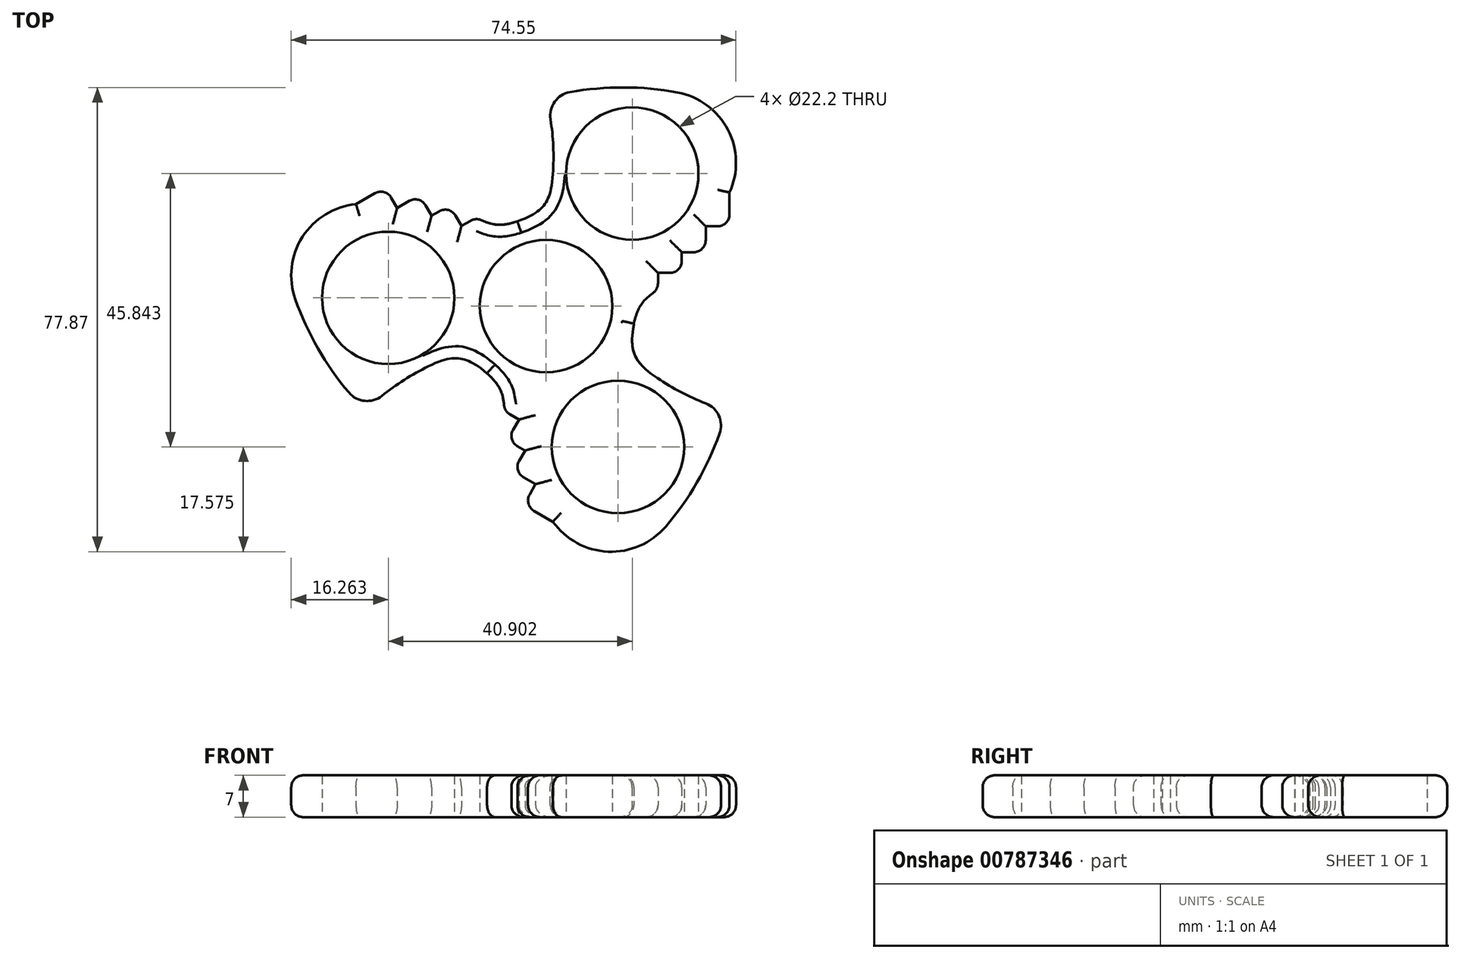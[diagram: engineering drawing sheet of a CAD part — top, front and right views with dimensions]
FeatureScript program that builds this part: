
annotation { "Feature Type Name" : "Feature", "Feature Type Description" : "" }
export const myFeature = defineFeature(function(context is Context, id is Id, definition is map)
    precondition{}
    {
        {
            var Q0;
            Q0=qCreatedBy(makeId("Top.planeOp"),FACE);
            var sketch = newSketch(context, id + "F0", { "sketchPlane" : qUnion([Q0])});
            skCircle(sketch, "E0", {"center": v(0, 0) * mm, "radius": 15 * mm});
            skArc(sketch, "E1", {"start": v(0, 15) * mm, "mid": v(1.23, 25) * mm, "end": v(0, 35) * mm});
            skPoint(sketch, "E2", {"position": v(0, 15) * mm});
            skPoint(sketch, "E3", {"position": v(0, 35) * mm});
            skPoint(sketch, "E4", {"position": v(36, 31) * mm});
            skArc(sketch, "E5.trimOffspring", {"start": v(36, 31) * mm, "mid": v(18.37, 36.37) * mm, "end": v(0, 35) * mm});
            skArc(sketch, "E6.trimOffspring", {"start": v(14.74, 2.75) * mm, "mid": v(27.95, 14.94) * mm, "end": v(36, 31) * mm});
            skCircle(sketch, "E7", {"center": v(0, 0) * mm, "radius": 11.1 * mm});
            skLineSegment(sketch, "E8", {"start": v(0, 15) * mm, "end": v(14.74, 2.75) * mm, "construction": true});
            skLineSegment(sketch, "E9", {"start": v(36, 31) * mm, "end": v(0, 35) * mm, "construction": true});
            skLineSegment(sketch, "E10", {"start": v(14.74, 2.75) * mm, "end": v(18.74, 2.75) * mm});
            skLineSegment(sketch, "E11", {"start": v(18.74, 2.75) * mm, "end": v(18.74, 5.57) * mm});
            skLineSegment(sketch, "E12", {"start": v(18.74, 5.57) * mm, "end": v(22.74, 5.57) * mm});
            skLineSegment(sketch, "E13", {"start": v(22.74, 5.57) * mm, "end": v(22.74, 9.04) * mm});
            skLineSegment(sketch, "E14", {"start": v(22.74, 9.04) * mm, "end": v(26.74, 9.04) * mm});
            skLineSegment(sketch, "E15", {"start": v(26.74, 9.04) * mm, "end": v(26.74, 13.4) * mm});
            skLineSegment(sketch, "E16", {"start": v(26.74, 13.4) * mm, "end": v(30.74, 13.4) * mm});
            skLineSegment(sketch, "E17", {"start": v(30.74, 13.4) * mm, "end": v(30.74, 19.06) * mm});
            skCircle(sketch, "E18", {"center": v(14.43, 22.23) * mm, "radius": 11.1 * mm});
            skLineSegment(sketch, "E19", {"start": v(0, 0) * mm, "end": v(21.2, 32.64) * mm, "construction": true});
            skPoint(sketch, "E20.1.0", {"position": v(-44.85, 15.68) * mm});
            skLineSegment(sketch, "E20.1.1", {"start": v(-44.85, 15.68) * mm, "end": v(-30.31, -17.5) * mm, "construction": true});
            skArc(sketch, "E20.1.2", {"start": v(-9.76, 11.4) * mm, "mid": v(-26.91, 16.74) * mm, "end": v(-44.85, 15.68) * mm});
            skLineSegment(sketch, "E20.1.3", {"start": v(-9.76, 11.4) * mm, "end": v(-11.76, 14.86) * mm});
            skPoint(sketch, "E20.1.4", {"position": v(-13, -7.5) * mm});
            skArc(sketch, "E20.1.5", {"start": v(-44.85, 15.68) * mm, "mid": v(-40.69, -2.27) * mm, "end": v(-30.31, -17.5) * mm});
            skPoint(sketch, "E20.1.7", {"position": v(-30.31, -17.5) * mm});
            skLineSegment(sketch, "E20.1.8", {"start": v(-13, -7.5) * mm, "end": v(-9.76, 11.4) * mm, "construction": true});
            skLineSegment(sketch, "E20.1.9", {"start": v(-26.97, 19.93) * mm, "end": v(-31.88, 17.1) * mm});
            skCircle(sketch, "E20.1.10", {"center": v(-26.47, 1.39) * mm, "radius": 11.1 * mm});
            skLineSegment(sketch, "E20.1.11", {"start": v(0, 0) * mm, "end": v(-38.87, 2.04) * mm, "construction": true});
            skArc(sketch, "E20.1.12", {"start": v(-13, -7.5) * mm, "mid": v(-22.27, -11.43) * mm, "end": v(-30.31, -17.5) * mm});
            skLineSegment(sketch, "E20.1.14", {"start": v(-19.2, 15.18) * mm, "end": v(-21.2, 18.64) * mm});
            skLineSegment(sketch, "E20.1.15", {"start": v(-14.2, 13.45) * mm, "end": v(-16.2, 16.91) * mm});
            skLineSegment(sketch, "E20.1.16", {"start": v(-16.2, 16.91) * mm, "end": v(-19.2, 15.18) * mm});
            skLineSegment(sketch, "E20.1.17", {"start": v(-11.76, 14.86) * mm, "end": v(-14.2, 13.45) * mm});
            skLineSegment(sketch, "E20.1.19", {"start": v(-24.97, 16.46) * mm, "end": v(-26.97, 19.93) * mm});
            skLineSegment(sketch, "E20.1.20", {"start": v(-21.2, 18.64) * mm, "end": v(-24.97, 16.46) * mm});
            skPoint(sketch, "E20.2.0", {"position": v(8.85, -46.68) * mm});
            skLineSegment(sketch, "E20.2.1", {"start": v(8.85, -46.68) * mm, "end": v(30.31, -17.5) * mm, "construction": true});
            skArc(sketch, "E20.2.2", {"start": v(-4.99, -14.15) * mm, "mid": v(-1.04, -31.68) * mm, "end": v(8.85, -46.68) * mm});
            skLineSegment(sketch, "E20.2.3", {"start": v(-4.99, -14.15) * mm, "end": v(-6.99, -17.61) * mm});
            skPoint(sketch, "E20.2.4", {"position": v(13, -7.5) * mm});
            skArc(sketch, "E20.2.5", {"start": v(8.85, -46.68) * mm, "mid": v(22.31, -34.1) * mm, "end": v(30.31, -17.5) * mm});
            skPoint(sketch, "E20.2.7", {"position": v(30.31, -17.5) * mm});
            skLineSegment(sketch, "E20.2.8", {"start": v(13, -7.5) * mm, "end": v(-4.99, -14.15) * mm, "construction": true});
            skLineSegment(sketch, "E20.2.9", {"start": v(-3.77, -33.32) * mm, "end": v(1.13, -36.16) * mm});
            skCircle(sketch, "E20.2.10", {"center": v(12.03, -23.61) * mm, "radius": 11.1 * mm});
            skLineSegment(sketch, "E20.2.11", {"start": v(0, 0) * mm, "end": v(17.67, -34.68) * mm, "construction": true});
            skArc(sketch, "E20.2.12", {"start": v(13, -7.5) * mm, "mid": v(21.04, -13.57) * mm, "end": v(30.31, -17.5) * mm});
            skLineSegment(sketch, "E20.2.14", {"start": v(-3.54, -24.22) * mm, "end": v(-5.54, -27.68) * mm});
            skLineSegment(sketch, "E20.2.15", {"start": v(-4.55, -19.02) * mm, "end": v(-6.55, -22.48) * mm});
            skLineSegment(sketch, "E20.2.16", {"start": v(-6.55, -22.48) * mm, "end": v(-3.54, -24.22) * mm});
            skLineSegment(sketch, "E20.2.17", {"start": v(-6.99, -17.61) * mm, "end": v(-4.55, -19.02) * mm});
            skLineSegment(sketch, "E20.2.19", {"start": v(-1.77, -29.86) * mm, "end": v(-3.77, -33.32) * mm});
            skLineSegment(sketch, "E20.2.20", {"start": v(-5.54, -27.68) * mm, "end": v(-1.77, -29.86) * mm});
            skSolve(sketch);
        }
        {
            var Q0;
            Q0=qSketchRegion(id+"F0",true);
            extrude(context, id + "F1", {"entities" : qUnion([Q0]), "depth" : 7 * mm, "offsetDistance" : 25 * mm});
        }
        {
            var Q0;
            Q0=makeQuery(id+"F1.opExtrude","SWEPT_EDGE",EDGE,{"disambiguationData":[OSD([sQuery(id+"F0.wireOp",EDGE,"E5.trimOffspring"),sQuery(id+"F0.wireOp",EDGE,"E6.trimOffspring")])]});
            var Q1;
            Q1=makeQuery(id+"F1.opExtrude","SWEPT_EDGE",EDGE,{"disambiguationData":[OSD([sQuery(id+"F0.wireOp",EDGE,"E20.2.2"),sQuery(id+"F0.wireOp",EDGE,"E20.2.5")])]});
            var Q2;
            Q2=makeQuery(id+"F1.opExtrude","SWEPT_EDGE",EDGE,{"disambiguationData":[OSD([sQuery(id+"F0.wireOp",EDGE,"E20.1.2"),sQuery(id+"F0.wireOp",EDGE,"E20.1.5")])]});
            fillet(context, id + "F2", {"entities" : qUnion([Q0, Q1, Q2]), "radius" : 12 * mm, "tangentPropagation" : true, "allowEdgeOverflow" : false});
        }
        {
            var Q0;
            Q0=makeQuery(id+"F1.opExtrude","SWEPT_EDGE",EDGE,{"disambiguationData":[OSD([sQuery(id+"F0.wireOp",EDGE,"E1"),sQuery(id+"F0.wireOp",EDGE,"E5.trimOffspring")])]});
            var Q1;
            Q1=makeQuery(id+"F1.opExtrude","SWEPT_EDGE",EDGE,{"disambiguationData":[OSD([sQuery(id+"F0.wireOp",EDGE,"E20.1.5"),sQuery(id+"F0.wireOp",EDGE,"E20.1.12")])]});
            var Q2;
            Q2=makeQuery(id+"F1.opExtrude","SWEPT_EDGE",EDGE,{"disambiguationData":[OSD([sQuery(id+"F0.wireOp",EDGE,"E20.2.5"),sQuery(id+"F0.wireOp",EDGE,"E20.2.12")])]});
            fillet(context, id + "F3", {"entities" : qUnion([Q0, Q1, Q2]), "radius" : 4 * mm, "tangentPropagation" : true, "allowEdgeOverflow" : false});
        }
        {
            var Q0;
            Q0=makeQuery(id+"F1.opExtrude","SWEPT_EDGE",EDGE,{"disambiguationData":[OSD([sQuery(id+"F0.wireOp",EDGE,"E0"),sQuery(id+"F0.wireOp",EDGE,"544d86c7-8deb-4338-a2d6-1758b23e3787.1.16")])]});
            var Q1;
            Q1=makeQuery(id+"F1.opExtrude","SWEPT_EDGE",EDGE,{"disambiguationData":[OSD([sQuery(id+"F0.wireOp",EDGE,"E0"),sQuery(id+"F0.wireOp",EDGE,"544d86c7-8deb-4338-a2d6-1758b23e3787.2.5")])]});
            var Q2;
            Q2=makeQuery(id+"F1.opExtrude","SWEPT_EDGE",EDGE,{"disambiguationData":[OSD([sQuery(id+"F0.wireOp",EDGE,"E0"),sQuery(id+"F0.wireOp",EDGE,"544d86c7-8deb-4338-a2d6-1758b23e3787.1.5")])]});
            var Q3;
            Q3=makeQuery(id+"F1.opExtrude","SWEPT_EDGE",EDGE,{"disambiguationData":[OSD([sQuery(id+"F0.wireOp",EDGE,"E0"),sQuery(id+"F0.wireOp",EDGE,"E1")])]});
            var Q4;
            Q4=makeQuery(id+"F1.opExtrude","SWEPT_EDGE",EDGE,{"disambiguationData":[OSD([sQuery(id+"F0.wireOp",EDGE,"E0"),sQuery(id+"F0.wireOp",EDGE,"E6.trimOffspring")])]});
            var Q5;
            Q5=makeQuery(id+"F1.opExtrude","SWEPT_EDGE",EDGE,{"disambiguationData":[OSD([sQuery(id+"F0.wireOp",EDGE,"E0"),sQuery(id+"F0.wireOp",EDGE,"544d86c7-8deb-4338-a2d6-1758b23e3787.2.16")])]});
            var Q6;
            Q6=makeQuery(id+"F1.opExtrude","SWEPT_EDGE",EDGE,{"disambiguationData":[OSD([sQuery(id+"F0.wireOp",EDGE,"E0"),sQuery(id+"F0.wireOp",EDGE,"E20.1.2"),sQuery(id+"F0.wireOp",EDGE,"E20.1.3")])]});
            var Q7;
            Q7=makeQuery(id+"F1.opExtrude","SWEPT_EDGE",EDGE,{"disambiguationData":[OSD([sQuery(id+"F0.wireOp",EDGE,"E0"),sQuery(id+"F0.wireOp",EDGE,"E20.2.2"),sQuery(id+"F0.wireOp",EDGE,"E20.2.3")])]});
            fillet(context, id + "F4", {"entities" : qUnion([Q0, Q1, Q2, Q3, Q4, Q5, Q6, Q7]), "radius" : 9.2 * mm, "rho" : .6, "crossSection" : FilletCrossSection.CONIC, "allowEdgeOverflow" : false});
        }
        {
            var Q0;
            {var subQ0=sQuery(id+"F0.wireOp",EDGE,"E1");var subQ1=sQuery(id+"F0.wireOp",EDGE,"E0");Q0=makeQuery(id+"F4.opFillet","BLEND_EDGE",EDGE,{"blendedFrom":[makeQuery(id+"F1.opExtrude","SWEPT_EDGE",EDGE,{"disambiguationData":[OSD([subQ1,subQ0])]}),makeQuery(id+"F1.opExtrude","CAP_FACE",FACE,{"disambiguationData":[OSD([subQ1,subQ0,sQuery(id+"F0.wireOp",EDGE,"E5.trimOffspring"),sQuery(id+"F0.wireOp",EDGE,"E6.trimOffspring"),sQuery(id+"F0.wireOp",EDGE,"E7"),sQuery(id+"F0.wireOp",EDGE,"E10"),sQuery(id+"F0.wireOp",EDGE,"E11"),sQuery(id+"F0.wireOp",EDGE,"E12"),sQuery(id+"F0.wireOp",EDGE,"E13"),sQuery(id+"F0.wireOp",EDGE,"E14"),sQuery(id+"F0.wireOp",EDGE,"E15"),sQuery(id+"F0.wireOp",EDGE,"E16"),sQuery(id+"F0.wireOp",EDGE,"E17"),sQuery(id+"F0.wireOp",EDGE,"E18"),sQuery(id+"F0.wireOp",EDGE,"E20.1.2"),sQuery(id+"F0.wireOp",EDGE,"E20.1.3"),sQuery(id+"F0.wireOp",EDGE,"E20.1.5"),sQuery(id+"F0.wireOp",EDGE,"E20.1.9"),sQuery(id+"F0.wireOp",EDGE,"E20.1.10"),sQuery(id+"F0.wireOp",EDGE,"E20.1.12"),sQuery(id+"F0.wireOp",EDGE,"E20.1.14"),sQuery(id+"F0.wireOp",EDGE,"E20.1.15"),sQuery(id+"F0.wireOp",EDGE,"E20.1.16"),sQuery(id+"F0.wireOp",EDGE,"E20.1.17"),sQuery(id+"F0.wireOp",EDGE,"E20.1.19"),sQuery(id+"F0.wireOp",EDGE,"E20.1.20"),sQuery(id+"F0.wireOp",EDGE,"E20.2.2"),sQuery(id+"F0.wireOp",EDGE,"E20.2.3"),sQuery(id+"F0.wireOp",EDGE,"E20.2.5"),sQuery(id+"F0.wireOp",EDGE,"E20.2.9"),sQuery(id+"F0.wireOp",EDGE,"E20.2.10"),sQuery(id+"F0.wireOp",EDGE,"E20.2.12"),sQuery(id+"F0.wireOp",EDGE,"E20.2.14"),sQuery(id+"F0.wireOp",EDGE,"E20.2.15"),sQuery(id+"F0.wireOp",EDGE,"E20.2.16"),sQuery(id+"F0.wireOp",EDGE,"E20.2.17"),sQuery(id+"F0.wireOp",EDGE,"E20.2.19"),sQuery(id+"F0.wireOp",EDGE,"E20.2.20")])],"isStart":false})],"blendedInto":[makeQuery(id+"F1.opExtrude","CAP_FACE",FACE,{"disambiguationData":[OSD([subQ1,subQ0,sQuery(id+"F0.wireOp",EDGE,"E5.trimOffspring"),sQuery(id+"F0.wireOp",EDGE,"E6.trimOffspring"),sQuery(id+"F0.wireOp",EDGE,"E7"),sQuery(id+"F0.wireOp",EDGE,"E10"),sQuery(id+"F0.wireOp",EDGE,"E11"),sQuery(id+"F0.wireOp",EDGE,"E12"),sQuery(id+"F0.wireOp",EDGE,"E13"),sQuery(id+"F0.wireOp",EDGE,"E14"),sQuery(id+"F0.wireOp",EDGE,"E15"),sQuery(id+"F0.wireOp",EDGE,"E16"),sQuery(id+"F0.wireOp",EDGE,"E17"),sQuery(id+"F0.wireOp",EDGE,"E18"),sQuery(id+"F0.wireOp",EDGE,"E20.1.2"),sQuery(id+"F0.wireOp",EDGE,"E20.1.3"),sQuery(id+"F0.wireOp",EDGE,"E20.1.5"),sQuery(id+"F0.wireOp",EDGE,"E20.1.9"),sQuery(id+"F0.wireOp",EDGE,"E20.1.10"),sQuery(id+"F0.wireOp",EDGE,"E20.1.12"),sQuery(id+"F0.wireOp",EDGE,"E20.1.14"),sQuery(id+"F0.wireOp",EDGE,"E20.1.15"),sQuery(id+"F0.wireOp",EDGE,"E20.1.16"),sQuery(id+"F0.wireOp",EDGE,"E20.1.17"),sQuery(id+"F0.wireOp",EDGE,"E20.1.19"),sQuery(id+"F0.wireOp",EDGE,"E20.1.20"),sQuery(id+"F0.wireOp",EDGE,"E20.2.2"),sQuery(id+"F0.wireOp",EDGE,"E20.2.3"),sQuery(id+"F0.wireOp",EDGE,"E20.2.5"),sQuery(id+"F0.wireOp",EDGE,"E20.2.9"),sQuery(id+"F0.wireOp",EDGE,"E20.2.10"),sQuery(id+"F0.wireOp",EDGE,"E20.2.12"),sQuery(id+"F0.wireOp",EDGE,"E20.2.14"),sQuery(id+"F0.wireOp",EDGE,"E20.2.15"),sQuery(id+"F0.wireOp",EDGE,"E20.2.16"),sQuery(id+"F0.wireOp",EDGE,"E20.2.17"),sQuery(id+"F0.wireOp",EDGE,"E20.2.19"),sQuery(id+"F0.wireOp",EDGE,"E20.2.20")])],"isStart":false})]});}
            var Q1;
            {var subQ0=sQuery(id+"F0.wireOp",EDGE,"E20.1.12");var subQ1=sQuery(id+"F0.wireOp",EDGE,"E0");Q1=makeQuery(id+"F4.opFillet","BLEND_EDGE",EDGE,{"blendedFrom":[makeQuery(id+"F1.opExtrude","SWEPT_EDGE",EDGE,{"disambiguationData":[OSD([subQ1,subQ0])]}),makeQuery(id+"F1.opExtrude","CAP_FACE",FACE,{"disambiguationData":[OSD([subQ1,sQuery(id+"F0.wireOp",EDGE,"E1"),sQuery(id+"F0.wireOp",EDGE,"E5.trimOffspring"),sQuery(id+"F0.wireOp",EDGE,"E6.trimOffspring"),sQuery(id+"F0.wireOp",EDGE,"E7"),sQuery(id+"F0.wireOp",EDGE,"E10"),sQuery(id+"F0.wireOp",EDGE,"E11"),sQuery(id+"F0.wireOp",EDGE,"E12"),sQuery(id+"F0.wireOp",EDGE,"E13"),sQuery(id+"F0.wireOp",EDGE,"E14"),sQuery(id+"F0.wireOp",EDGE,"E15"),sQuery(id+"F0.wireOp",EDGE,"E16"),sQuery(id+"F0.wireOp",EDGE,"E17"),sQuery(id+"F0.wireOp",EDGE,"E18"),sQuery(id+"F0.wireOp",EDGE,"E20.1.2"),sQuery(id+"F0.wireOp",EDGE,"E20.1.3"),sQuery(id+"F0.wireOp",EDGE,"E20.1.5"),sQuery(id+"F0.wireOp",EDGE,"E20.1.9"),sQuery(id+"F0.wireOp",EDGE,"E20.1.10"),subQ0,sQuery(id+"F0.wireOp",EDGE,"E20.1.14"),sQuery(id+"F0.wireOp",EDGE,"E20.1.15"),sQuery(id+"F0.wireOp",EDGE,"E20.1.16"),sQuery(id+"F0.wireOp",EDGE,"E20.1.17"),sQuery(id+"F0.wireOp",EDGE,"E20.1.19"),sQuery(id+"F0.wireOp",EDGE,"E20.1.20"),sQuery(id+"F0.wireOp",EDGE,"E20.2.2"),sQuery(id+"F0.wireOp",EDGE,"E20.2.3"),sQuery(id+"F0.wireOp",EDGE,"E20.2.5"),sQuery(id+"F0.wireOp",EDGE,"E20.2.9"),sQuery(id+"F0.wireOp",EDGE,"E20.2.10"),sQuery(id+"F0.wireOp",EDGE,"E20.2.12"),sQuery(id+"F0.wireOp",EDGE,"E20.2.14"),sQuery(id+"F0.wireOp",EDGE,"E20.2.15"),sQuery(id+"F0.wireOp",EDGE,"E20.2.16"),sQuery(id+"F0.wireOp",EDGE,"E20.2.17"),sQuery(id+"F0.wireOp",EDGE,"E20.2.19"),sQuery(id+"F0.wireOp",EDGE,"E20.2.20")])],"isStart":false})],"blendedInto":[makeQuery(id+"F1.opExtrude","CAP_FACE",FACE,{"disambiguationData":[OSD([subQ1,sQuery(id+"F0.wireOp",EDGE,"E1"),sQuery(id+"F0.wireOp",EDGE,"E5.trimOffspring"),sQuery(id+"F0.wireOp",EDGE,"E6.trimOffspring"),sQuery(id+"F0.wireOp",EDGE,"E7"),sQuery(id+"F0.wireOp",EDGE,"E10"),sQuery(id+"F0.wireOp",EDGE,"E11"),sQuery(id+"F0.wireOp",EDGE,"E12"),sQuery(id+"F0.wireOp",EDGE,"E13"),sQuery(id+"F0.wireOp",EDGE,"E14"),sQuery(id+"F0.wireOp",EDGE,"E15"),sQuery(id+"F0.wireOp",EDGE,"E16"),sQuery(id+"F0.wireOp",EDGE,"E17"),sQuery(id+"F0.wireOp",EDGE,"E18"),sQuery(id+"F0.wireOp",EDGE,"E20.1.2"),sQuery(id+"F0.wireOp",EDGE,"E20.1.3"),sQuery(id+"F0.wireOp",EDGE,"E20.1.5"),sQuery(id+"F0.wireOp",EDGE,"E20.1.9"),sQuery(id+"F0.wireOp",EDGE,"E20.1.10"),subQ0,sQuery(id+"F0.wireOp",EDGE,"E20.1.14"),sQuery(id+"F0.wireOp",EDGE,"E20.1.15"),sQuery(id+"F0.wireOp",EDGE,"E20.1.16"),sQuery(id+"F0.wireOp",EDGE,"E20.1.17"),sQuery(id+"F0.wireOp",EDGE,"E20.1.19"),sQuery(id+"F0.wireOp",EDGE,"E20.1.20"),sQuery(id+"F0.wireOp",EDGE,"E20.2.2"),sQuery(id+"F0.wireOp",EDGE,"E20.2.3"),sQuery(id+"F0.wireOp",EDGE,"E20.2.5"),sQuery(id+"F0.wireOp",EDGE,"E20.2.9"),sQuery(id+"F0.wireOp",EDGE,"E20.2.10"),sQuery(id+"F0.wireOp",EDGE,"E20.2.12"),sQuery(id+"F0.wireOp",EDGE,"E20.2.14"),sQuery(id+"F0.wireOp",EDGE,"E20.2.15"),sQuery(id+"F0.wireOp",EDGE,"E20.2.16"),sQuery(id+"F0.wireOp",EDGE,"E20.2.17"),sQuery(id+"F0.wireOp",EDGE,"E20.2.19"),sQuery(id+"F0.wireOp",EDGE,"E20.2.20")])],"isStart":false})]});}
            var Q2;
            {var subQ0=sQuery(id+"F0.wireOp",EDGE,"E20.2.12");var subQ1=sQuery(id+"F0.wireOp",EDGE,"E0");Q2=makeQuery(id+"F4.opFillet","BLEND_EDGE",EDGE,{"blendedFrom":[makeQuery(id+"F1.opExtrude","SWEPT_EDGE",EDGE,{"disambiguationData":[OSD([subQ1,subQ0])]}),makeQuery(id+"F1.opExtrude","CAP_FACE",FACE,{"disambiguationData":[OSD([subQ1,sQuery(id+"F0.wireOp",EDGE,"E1"),sQuery(id+"F0.wireOp",EDGE,"E5.trimOffspring"),sQuery(id+"F0.wireOp",EDGE,"E6.trimOffspring"),sQuery(id+"F0.wireOp",EDGE,"E7"),sQuery(id+"F0.wireOp",EDGE,"E10"),sQuery(id+"F0.wireOp",EDGE,"E11"),sQuery(id+"F0.wireOp",EDGE,"E12"),sQuery(id+"F0.wireOp",EDGE,"E13"),sQuery(id+"F0.wireOp",EDGE,"E14"),sQuery(id+"F0.wireOp",EDGE,"E15"),sQuery(id+"F0.wireOp",EDGE,"E16"),sQuery(id+"F0.wireOp",EDGE,"E17"),sQuery(id+"F0.wireOp",EDGE,"E18"),sQuery(id+"F0.wireOp",EDGE,"E20.1.2"),sQuery(id+"F0.wireOp",EDGE,"E20.1.3"),sQuery(id+"F0.wireOp",EDGE,"E20.1.5"),sQuery(id+"F0.wireOp",EDGE,"E20.1.9"),sQuery(id+"F0.wireOp",EDGE,"E20.1.10"),sQuery(id+"F0.wireOp",EDGE,"E20.1.12"),sQuery(id+"F0.wireOp",EDGE,"E20.1.14"),sQuery(id+"F0.wireOp",EDGE,"E20.1.15"),sQuery(id+"F0.wireOp",EDGE,"E20.1.16"),sQuery(id+"F0.wireOp",EDGE,"E20.1.17"),sQuery(id+"F0.wireOp",EDGE,"E20.1.19"),sQuery(id+"F0.wireOp",EDGE,"E20.1.20"),sQuery(id+"F0.wireOp",EDGE,"E20.2.2"),sQuery(id+"F0.wireOp",EDGE,"E20.2.3"),sQuery(id+"F0.wireOp",EDGE,"E20.2.5"),sQuery(id+"F0.wireOp",EDGE,"E20.2.9"),sQuery(id+"F0.wireOp",EDGE,"E20.2.10"),subQ0,sQuery(id+"F0.wireOp",EDGE,"E20.2.14"),sQuery(id+"F0.wireOp",EDGE,"E20.2.15"),sQuery(id+"F0.wireOp",EDGE,"E20.2.16"),sQuery(id+"F0.wireOp",EDGE,"E20.2.17"),sQuery(id+"F0.wireOp",EDGE,"E20.2.19"),sQuery(id+"F0.wireOp",EDGE,"E20.2.20")])],"isStart":false})],"blendedInto":[makeQuery(id+"F1.opExtrude","CAP_FACE",FACE,{"disambiguationData":[OSD([subQ1,sQuery(id+"F0.wireOp",EDGE,"E1"),sQuery(id+"F0.wireOp",EDGE,"E5.trimOffspring"),sQuery(id+"F0.wireOp",EDGE,"E6.trimOffspring"),sQuery(id+"F0.wireOp",EDGE,"E7"),sQuery(id+"F0.wireOp",EDGE,"E10"),sQuery(id+"F0.wireOp",EDGE,"E11"),sQuery(id+"F0.wireOp",EDGE,"E12"),sQuery(id+"F0.wireOp",EDGE,"E13"),sQuery(id+"F0.wireOp",EDGE,"E14"),sQuery(id+"F0.wireOp",EDGE,"E15"),sQuery(id+"F0.wireOp",EDGE,"E16"),sQuery(id+"F0.wireOp",EDGE,"E17"),sQuery(id+"F0.wireOp",EDGE,"E18"),sQuery(id+"F0.wireOp",EDGE,"E20.1.2"),sQuery(id+"F0.wireOp",EDGE,"E20.1.3"),sQuery(id+"F0.wireOp",EDGE,"E20.1.5"),sQuery(id+"F0.wireOp",EDGE,"E20.1.9"),sQuery(id+"F0.wireOp",EDGE,"E20.1.10"),sQuery(id+"F0.wireOp",EDGE,"E20.1.12"),sQuery(id+"F0.wireOp",EDGE,"E20.1.14"),sQuery(id+"F0.wireOp",EDGE,"E20.1.15"),sQuery(id+"F0.wireOp",EDGE,"E20.1.16"),sQuery(id+"F0.wireOp",EDGE,"E20.1.17"),sQuery(id+"F0.wireOp",EDGE,"E20.1.19"),sQuery(id+"F0.wireOp",EDGE,"E20.1.20"),sQuery(id+"F0.wireOp",EDGE,"E20.2.2"),sQuery(id+"F0.wireOp",EDGE,"E20.2.3"),sQuery(id+"F0.wireOp",EDGE,"E20.2.5"),sQuery(id+"F0.wireOp",EDGE,"E20.2.9"),sQuery(id+"F0.wireOp",EDGE,"E20.2.10"),subQ0,sQuery(id+"F0.wireOp",EDGE,"E20.2.14"),sQuery(id+"F0.wireOp",EDGE,"E20.2.15"),sQuery(id+"F0.wireOp",EDGE,"E20.2.16"),sQuery(id+"F0.wireOp",EDGE,"E20.2.17"),sQuery(id+"F0.wireOp",EDGE,"E20.2.19"),sQuery(id+"F0.wireOp",EDGE,"E20.2.20")])],"isStart":false})]});}
            var Q3;
            {var subQ0=sQuery(id+"F0.wireOp",EDGE,"E1");var subQ1=sQuery(id+"F0.wireOp",EDGE,"E0");Q3=makeQuery(id+"F4.opFillet","BLEND_EDGE",EDGE,{"blendedFrom":[makeQuery(id+"F1.opExtrude","SWEPT_EDGE",EDGE,{"disambiguationData":[OSD([subQ1,subQ0])]}),makeQuery(id+"F1.opExtrude","CAP_FACE",FACE,{"disambiguationData":[OSD([subQ1,subQ0,sQuery(id+"F0.wireOp",EDGE,"E5.trimOffspring"),sQuery(id+"F0.wireOp",EDGE,"E6.trimOffspring"),sQuery(id+"F0.wireOp",EDGE,"E7"),sQuery(id+"F0.wireOp",EDGE,"E10"),sQuery(id+"F0.wireOp",EDGE,"E11"),sQuery(id+"F0.wireOp",EDGE,"E12"),sQuery(id+"F0.wireOp",EDGE,"E13"),sQuery(id+"F0.wireOp",EDGE,"E14"),sQuery(id+"F0.wireOp",EDGE,"E15"),sQuery(id+"F0.wireOp",EDGE,"E16"),sQuery(id+"F0.wireOp",EDGE,"E17"),sQuery(id+"F0.wireOp",EDGE,"E18"),sQuery(id+"F0.wireOp",EDGE,"E20.1.2"),sQuery(id+"F0.wireOp",EDGE,"E20.1.3"),sQuery(id+"F0.wireOp",EDGE,"E20.1.5"),sQuery(id+"F0.wireOp",EDGE,"E20.1.9"),sQuery(id+"F0.wireOp",EDGE,"E20.1.10"),sQuery(id+"F0.wireOp",EDGE,"E20.1.12"),sQuery(id+"F0.wireOp",EDGE,"E20.1.14"),sQuery(id+"F0.wireOp",EDGE,"E20.1.15"),sQuery(id+"F0.wireOp",EDGE,"E20.1.16"),sQuery(id+"F0.wireOp",EDGE,"E20.1.17"),sQuery(id+"F0.wireOp",EDGE,"E20.1.19"),sQuery(id+"F0.wireOp",EDGE,"E20.1.20"),sQuery(id+"F0.wireOp",EDGE,"E20.2.2"),sQuery(id+"F0.wireOp",EDGE,"E20.2.3"),sQuery(id+"F0.wireOp",EDGE,"E20.2.5"),sQuery(id+"F0.wireOp",EDGE,"E20.2.9"),sQuery(id+"F0.wireOp",EDGE,"E20.2.10"),sQuery(id+"F0.wireOp",EDGE,"E20.2.12"),sQuery(id+"F0.wireOp",EDGE,"E20.2.14"),sQuery(id+"F0.wireOp",EDGE,"E20.2.15"),sQuery(id+"F0.wireOp",EDGE,"E20.2.16"),sQuery(id+"F0.wireOp",EDGE,"E20.2.17"),sQuery(id+"F0.wireOp",EDGE,"E20.2.19"),sQuery(id+"F0.wireOp",EDGE,"E20.2.20")])],"isStart":true})],"blendedInto":[makeQuery(id+"F1.opExtrude","CAP_FACE",FACE,{"disambiguationData":[OSD([subQ1,subQ0,sQuery(id+"F0.wireOp",EDGE,"E5.trimOffspring"),sQuery(id+"F0.wireOp",EDGE,"E6.trimOffspring"),sQuery(id+"F0.wireOp",EDGE,"E7"),sQuery(id+"F0.wireOp",EDGE,"E10"),sQuery(id+"F0.wireOp",EDGE,"E11"),sQuery(id+"F0.wireOp",EDGE,"E12"),sQuery(id+"F0.wireOp",EDGE,"E13"),sQuery(id+"F0.wireOp",EDGE,"E14"),sQuery(id+"F0.wireOp",EDGE,"E15"),sQuery(id+"F0.wireOp",EDGE,"E16"),sQuery(id+"F0.wireOp",EDGE,"E17"),sQuery(id+"F0.wireOp",EDGE,"E18"),sQuery(id+"F0.wireOp",EDGE,"E20.1.2"),sQuery(id+"F0.wireOp",EDGE,"E20.1.3"),sQuery(id+"F0.wireOp",EDGE,"E20.1.5"),sQuery(id+"F0.wireOp",EDGE,"E20.1.9"),sQuery(id+"F0.wireOp",EDGE,"E20.1.10"),sQuery(id+"F0.wireOp",EDGE,"E20.1.12"),sQuery(id+"F0.wireOp",EDGE,"E20.1.14"),sQuery(id+"F0.wireOp",EDGE,"E20.1.15"),sQuery(id+"F0.wireOp",EDGE,"E20.1.16"),sQuery(id+"F0.wireOp",EDGE,"E20.1.17"),sQuery(id+"F0.wireOp",EDGE,"E20.1.19"),sQuery(id+"F0.wireOp",EDGE,"E20.1.20"),sQuery(id+"F0.wireOp",EDGE,"E20.2.2"),sQuery(id+"F0.wireOp",EDGE,"E20.2.3"),sQuery(id+"F0.wireOp",EDGE,"E20.2.5"),sQuery(id+"F0.wireOp",EDGE,"E20.2.9"),sQuery(id+"F0.wireOp",EDGE,"E20.2.10"),sQuery(id+"F0.wireOp",EDGE,"E20.2.12"),sQuery(id+"F0.wireOp",EDGE,"E20.2.14"),sQuery(id+"F0.wireOp",EDGE,"E20.2.15"),sQuery(id+"F0.wireOp",EDGE,"E20.2.16"),sQuery(id+"F0.wireOp",EDGE,"E20.2.17"),sQuery(id+"F0.wireOp",EDGE,"E20.2.19"),sQuery(id+"F0.wireOp",EDGE,"E20.2.20")])],"isStart":true})]});}
            var Q4;
            {var subQ0=sQuery(id+"F0.wireOp",EDGE,"E20.1.12");var subQ1=sQuery(id+"F0.wireOp",EDGE,"E0");Q4=makeQuery(id+"F4.opFillet","BLEND_EDGE",EDGE,{"blendedFrom":[makeQuery(id+"F1.opExtrude","SWEPT_EDGE",EDGE,{"disambiguationData":[OSD([subQ1,subQ0])]}),makeQuery(id+"F1.opExtrude","CAP_FACE",FACE,{"disambiguationData":[OSD([subQ1,sQuery(id+"F0.wireOp",EDGE,"E1"),sQuery(id+"F0.wireOp",EDGE,"E5.trimOffspring"),sQuery(id+"F0.wireOp",EDGE,"E6.trimOffspring"),sQuery(id+"F0.wireOp",EDGE,"E7"),sQuery(id+"F0.wireOp",EDGE,"E10"),sQuery(id+"F0.wireOp",EDGE,"E11"),sQuery(id+"F0.wireOp",EDGE,"E12"),sQuery(id+"F0.wireOp",EDGE,"E13"),sQuery(id+"F0.wireOp",EDGE,"E14"),sQuery(id+"F0.wireOp",EDGE,"E15"),sQuery(id+"F0.wireOp",EDGE,"E16"),sQuery(id+"F0.wireOp",EDGE,"E17"),sQuery(id+"F0.wireOp",EDGE,"E18"),sQuery(id+"F0.wireOp",EDGE,"E20.1.2"),sQuery(id+"F0.wireOp",EDGE,"E20.1.3"),sQuery(id+"F0.wireOp",EDGE,"E20.1.5"),sQuery(id+"F0.wireOp",EDGE,"E20.1.9"),sQuery(id+"F0.wireOp",EDGE,"E20.1.10"),subQ0,sQuery(id+"F0.wireOp",EDGE,"E20.1.14"),sQuery(id+"F0.wireOp",EDGE,"E20.1.15"),sQuery(id+"F0.wireOp",EDGE,"E20.1.16"),sQuery(id+"F0.wireOp",EDGE,"E20.1.17"),sQuery(id+"F0.wireOp",EDGE,"E20.1.19"),sQuery(id+"F0.wireOp",EDGE,"E20.1.20"),sQuery(id+"F0.wireOp",EDGE,"E20.2.2"),sQuery(id+"F0.wireOp",EDGE,"E20.2.3"),sQuery(id+"F0.wireOp",EDGE,"E20.2.5"),sQuery(id+"F0.wireOp",EDGE,"E20.2.9"),sQuery(id+"F0.wireOp",EDGE,"E20.2.10"),sQuery(id+"F0.wireOp",EDGE,"E20.2.12"),sQuery(id+"F0.wireOp",EDGE,"E20.2.14"),sQuery(id+"F0.wireOp",EDGE,"E20.2.15"),sQuery(id+"F0.wireOp",EDGE,"E20.2.16"),sQuery(id+"F0.wireOp",EDGE,"E20.2.17"),sQuery(id+"F0.wireOp",EDGE,"E20.2.19"),sQuery(id+"F0.wireOp",EDGE,"E20.2.20")])],"isStart":true})],"blendedInto":[makeQuery(id+"F1.opExtrude","CAP_FACE",FACE,{"disambiguationData":[OSD([subQ1,sQuery(id+"F0.wireOp",EDGE,"E1"),sQuery(id+"F0.wireOp",EDGE,"E5.trimOffspring"),sQuery(id+"F0.wireOp",EDGE,"E6.trimOffspring"),sQuery(id+"F0.wireOp",EDGE,"E7"),sQuery(id+"F0.wireOp",EDGE,"E10"),sQuery(id+"F0.wireOp",EDGE,"E11"),sQuery(id+"F0.wireOp",EDGE,"E12"),sQuery(id+"F0.wireOp",EDGE,"E13"),sQuery(id+"F0.wireOp",EDGE,"E14"),sQuery(id+"F0.wireOp",EDGE,"E15"),sQuery(id+"F0.wireOp",EDGE,"E16"),sQuery(id+"F0.wireOp",EDGE,"E17"),sQuery(id+"F0.wireOp",EDGE,"E18"),sQuery(id+"F0.wireOp",EDGE,"E20.1.2"),sQuery(id+"F0.wireOp",EDGE,"E20.1.3"),sQuery(id+"F0.wireOp",EDGE,"E20.1.5"),sQuery(id+"F0.wireOp",EDGE,"E20.1.9"),sQuery(id+"F0.wireOp",EDGE,"E20.1.10"),subQ0,sQuery(id+"F0.wireOp",EDGE,"E20.1.14"),sQuery(id+"F0.wireOp",EDGE,"E20.1.15"),sQuery(id+"F0.wireOp",EDGE,"E20.1.16"),sQuery(id+"F0.wireOp",EDGE,"E20.1.17"),sQuery(id+"F0.wireOp",EDGE,"E20.1.19"),sQuery(id+"F0.wireOp",EDGE,"E20.1.20"),sQuery(id+"F0.wireOp",EDGE,"E20.2.2"),sQuery(id+"F0.wireOp",EDGE,"E20.2.3"),sQuery(id+"F0.wireOp",EDGE,"E20.2.5"),sQuery(id+"F0.wireOp",EDGE,"E20.2.9"),sQuery(id+"F0.wireOp",EDGE,"E20.2.10"),sQuery(id+"F0.wireOp",EDGE,"E20.2.12"),sQuery(id+"F0.wireOp",EDGE,"E20.2.14"),sQuery(id+"F0.wireOp",EDGE,"E20.2.15"),sQuery(id+"F0.wireOp",EDGE,"E20.2.16"),sQuery(id+"F0.wireOp",EDGE,"E20.2.17"),sQuery(id+"F0.wireOp",EDGE,"E20.2.19"),sQuery(id+"F0.wireOp",EDGE,"E20.2.20")])],"isStart":true})]});}
            var Q5;
            {var subQ0=sQuery(id+"F0.wireOp",EDGE,"E20.2.12");var subQ1=sQuery(id+"F0.wireOp",EDGE,"E0");Q5=makeQuery(id+"F4.opFillet","BLEND_EDGE",EDGE,{"blendedFrom":[makeQuery(id+"F1.opExtrude","SWEPT_EDGE",EDGE,{"disambiguationData":[OSD([subQ1,subQ0])]}),makeQuery(id+"F1.opExtrude","CAP_FACE",FACE,{"disambiguationData":[OSD([subQ1,sQuery(id+"F0.wireOp",EDGE,"E1"),sQuery(id+"F0.wireOp",EDGE,"E5.trimOffspring"),sQuery(id+"F0.wireOp",EDGE,"E6.trimOffspring"),sQuery(id+"F0.wireOp",EDGE,"E7"),sQuery(id+"F0.wireOp",EDGE,"E10"),sQuery(id+"F0.wireOp",EDGE,"E11"),sQuery(id+"F0.wireOp",EDGE,"E12"),sQuery(id+"F0.wireOp",EDGE,"E13"),sQuery(id+"F0.wireOp",EDGE,"E14"),sQuery(id+"F0.wireOp",EDGE,"E15"),sQuery(id+"F0.wireOp",EDGE,"E16"),sQuery(id+"F0.wireOp",EDGE,"E17"),sQuery(id+"F0.wireOp",EDGE,"E18"),sQuery(id+"F0.wireOp",EDGE,"E20.1.2"),sQuery(id+"F0.wireOp",EDGE,"E20.1.3"),sQuery(id+"F0.wireOp",EDGE,"E20.1.5"),sQuery(id+"F0.wireOp",EDGE,"E20.1.9"),sQuery(id+"F0.wireOp",EDGE,"E20.1.10"),sQuery(id+"F0.wireOp",EDGE,"E20.1.12"),sQuery(id+"F0.wireOp",EDGE,"E20.1.14"),sQuery(id+"F0.wireOp",EDGE,"E20.1.15"),sQuery(id+"F0.wireOp",EDGE,"E20.1.16"),sQuery(id+"F0.wireOp",EDGE,"E20.1.17"),sQuery(id+"F0.wireOp",EDGE,"E20.1.19"),sQuery(id+"F0.wireOp",EDGE,"E20.1.20"),sQuery(id+"F0.wireOp",EDGE,"E20.2.2"),sQuery(id+"F0.wireOp",EDGE,"E20.2.3"),sQuery(id+"F0.wireOp",EDGE,"E20.2.5"),sQuery(id+"F0.wireOp",EDGE,"E20.2.9"),sQuery(id+"F0.wireOp",EDGE,"E20.2.10"),subQ0,sQuery(id+"F0.wireOp",EDGE,"E20.2.14"),sQuery(id+"F0.wireOp",EDGE,"E20.2.15"),sQuery(id+"F0.wireOp",EDGE,"E20.2.16"),sQuery(id+"F0.wireOp",EDGE,"E20.2.17"),sQuery(id+"F0.wireOp",EDGE,"E20.2.19"),sQuery(id+"F0.wireOp",EDGE,"E20.2.20")])],"isStart":true})],"blendedInto":[makeQuery(id+"F1.opExtrude","CAP_FACE",FACE,{"disambiguationData":[OSD([subQ1,sQuery(id+"F0.wireOp",EDGE,"E1"),sQuery(id+"F0.wireOp",EDGE,"E5.trimOffspring"),sQuery(id+"F0.wireOp",EDGE,"E6.trimOffspring"),sQuery(id+"F0.wireOp",EDGE,"E7"),sQuery(id+"F0.wireOp",EDGE,"E10"),sQuery(id+"F0.wireOp",EDGE,"E11"),sQuery(id+"F0.wireOp",EDGE,"E12"),sQuery(id+"F0.wireOp",EDGE,"E13"),sQuery(id+"F0.wireOp",EDGE,"E14"),sQuery(id+"F0.wireOp",EDGE,"E15"),sQuery(id+"F0.wireOp",EDGE,"E16"),sQuery(id+"F0.wireOp",EDGE,"E17"),sQuery(id+"F0.wireOp",EDGE,"E18"),sQuery(id+"F0.wireOp",EDGE,"E20.1.2"),sQuery(id+"F0.wireOp",EDGE,"E20.1.3"),sQuery(id+"F0.wireOp",EDGE,"E20.1.5"),sQuery(id+"F0.wireOp",EDGE,"E20.1.9"),sQuery(id+"F0.wireOp",EDGE,"E20.1.10"),sQuery(id+"F0.wireOp",EDGE,"E20.1.12"),sQuery(id+"F0.wireOp",EDGE,"E20.1.14"),sQuery(id+"F0.wireOp",EDGE,"E20.1.15"),sQuery(id+"F0.wireOp",EDGE,"E20.1.16"),sQuery(id+"F0.wireOp",EDGE,"E20.1.17"),sQuery(id+"F0.wireOp",EDGE,"E20.1.19"),sQuery(id+"F0.wireOp",EDGE,"E20.1.20"),sQuery(id+"F0.wireOp",EDGE,"E20.2.2"),sQuery(id+"F0.wireOp",EDGE,"E20.2.3"),sQuery(id+"F0.wireOp",EDGE,"E20.2.5"),sQuery(id+"F0.wireOp",EDGE,"E20.2.9"),sQuery(id+"F0.wireOp",EDGE,"E20.2.10"),subQ0,sQuery(id+"F0.wireOp",EDGE,"E20.2.14"),sQuery(id+"F0.wireOp",EDGE,"E20.2.15"),sQuery(id+"F0.wireOp",EDGE,"E20.2.16"),sQuery(id+"F0.wireOp",EDGE,"E20.2.17"),sQuery(id+"F0.wireOp",EDGE,"E20.2.19"),sQuery(id+"F0.wireOp",EDGE,"E20.2.20")])],"isStart":true})]});}
            var Q6;
            {var subQ0=sQuery(id+"F0.wireOp",EDGE,"E10");var subQ1=sQuery(id+"F0.wireOp",EDGE,"E6.trimOffspring");var subQ2=sQuery(id+"F0.wireOp",EDGE,"E0");Q6=makeQuery(id+"F4.opFillet","BLEND_EDGE",EDGE,{"blendedFrom":[makeQuery(id+"F1.opExtrude","SWEPT_EDGE",EDGE,{"disambiguationData":[OSD([subQ2,subQ1,subQ0])]}),makeQuery(id+"F1.opExtrude","CAP_FACE",FACE,{"disambiguationData":[OSD([subQ2,sQuery(id+"F0.wireOp",EDGE,"E1"),sQuery(id+"F0.wireOp",EDGE,"E5.trimOffspring"),subQ1,sQuery(id+"F0.wireOp",EDGE,"E7"),subQ0,sQuery(id+"F0.wireOp",EDGE,"E11"),sQuery(id+"F0.wireOp",EDGE,"E12"),sQuery(id+"F0.wireOp",EDGE,"E13"),sQuery(id+"F0.wireOp",EDGE,"E14"),sQuery(id+"F0.wireOp",EDGE,"E15"),sQuery(id+"F0.wireOp",EDGE,"E16"),sQuery(id+"F0.wireOp",EDGE,"E17"),sQuery(id+"F0.wireOp",EDGE,"E18"),sQuery(id+"F0.wireOp",EDGE,"E20.1.2"),sQuery(id+"F0.wireOp",EDGE,"E20.1.3"),sQuery(id+"F0.wireOp",EDGE,"E20.1.5"),sQuery(id+"F0.wireOp",EDGE,"E20.1.9"),sQuery(id+"F0.wireOp",EDGE,"E20.1.10"),sQuery(id+"F0.wireOp",EDGE,"E20.1.12"),sQuery(id+"F0.wireOp",EDGE,"E20.1.14"),sQuery(id+"F0.wireOp",EDGE,"E20.1.15"),sQuery(id+"F0.wireOp",EDGE,"E20.1.16"),sQuery(id+"F0.wireOp",EDGE,"E20.1.17"),sQuery(id+"F0.wireOp",EDGE,"E20.1.19"),sQuery(id+"F0.wireOp",EDGE,"E20.1.20"),sQuery(id+"F0.wireOp",EDGE,"E20.2.2"),sQuery(id+"F0.wireOp",EDGE,"E20.2.3"),sQuery(id+"F0.wireOp",EDGE,"E20.2.5"),sQuery(id+"F0.wireOp",EDGE,"E20.2.9"),sQuery(id+"F0.wireOp",EDGE,"E20.2.10"),sQuery(id+"F0.wireOp",EDGE,"E20.2.12"),sQuery(id+"F0.wireOp",EDGE,"E20.2.14"),sQuery(id+"F0.wireOp",EDGE,"E20.2.15"),sQuery(id+"F0.wireOp",EDGE,"E20.2.16"),sQuery(id+"F0.wireOp",EDGE,"E20.2.17"),sQuery(id+"F0.wireOp",EDGE,"E20.2.19"),sQuery(id+"F0.wireOp",EDGE,"E20.2.20")])],"isStart":false})],"blendedInto":[makeQuery(id+"F1.opExtrude","CAP_FACE",FACE,{"disambiguationData":[OSD([subQ2,sQuery(id+"F0.wireOp",EDGE,"E1"),sQuery(id+"F0.wireOp",EDGE,"E5.trimOffspring"),subQ1,sQuery(id+"F0.wireOp",EDGE,"E7"),subQ0,sQuery(id+"F0.wireOp",EDGE,"E11"),sQuery(id+"F0.wireOp",EDGE,"E12"),sQuery(id+"F0.wireOp",EDGE,"E13"),sQuery(id+"F0.wireOp",EDGE,"E14"),sQuery(id+"F0.wireOp",EDGE,"E15"),sQuery(id+"F0.wireOp",EDGE,"E16"),sQuery(id+"F0.wireOp",EDGE,"E17"),sQuery(id+"F0.wireOp",EDGE,"E18"),sQuery(id+"F0.wireOp",EDGE,"E20.1.2"),sQuery(id+"F0.wireOp",EDGE,"E20.1.3"),sQuery(id+"F0.wireOp",EDGE,"E20.1.5"),sQuery(id+"F0.wireOp",EDGE,"E20.1.9"),sQuery(id+"F0.wireOp",EDGE,"E20.1.10"),sQuery(id+"F0.wireOp",EDGE,"E20.1.12"),sQuery(id+"F0.wireOp",EDGE,"E20.1.14"),sQuery(id+"F0.wireOp",EDGE,"E20.1.15"),sQuery(id+"F0.wireOp",EDGE,"E20.1.16"),sQuery(id+"F0.wireOp",EDGE,"E20.1.17"),sQuery(id+"F0.wireOp",EDGE,"E20.1.19"),sQuery(id+"F0.wireOp",EDGE,"E20.1.20"),sQuery(id+"F0.wireOp",EDGE,"E20.2.2"),sQuery(id+"F0.wireOp",EDGE,"E20.2.3"),sQuery(id+"F0.wireOp",EDGE,"E20.2.5"),sQuery(id+"F0.wireOp",EDGE,"E20.2.9"),sQuery(id+"F0.wireOp",EDGE,"E20.2.10"),sQuery(id+"F0.wireOp",EDGE,"E20.2.12"),sQuery(id+"F0.wireOp",EDGE,"E20.2.14"),sQuery(id+"F0.wireOp",EDGE,"E20.2.15"),sQuery(id+"F0.wireOp",EDGE,"E20.2.16"),sQuery(id+"F0.wireOp",EDGE,"E20.2.17"),sQuery(id+"F0.wireOp",EDGE,"E20.2.19"),sQuery(id+"F0.wireOp",EDGE,"E20.2.20")])],"isStart":false})]});}
            var Q7;
            {var subQ0=sQuery(id+"F0.wireOp",EDGE,"E10");var subQ1=sQuery(id+"F0.wireOp",EDGE,"E6.trimOffspring");var subQ2=sQuery(id+"F0.wireOp",EDGE,"E0");Q7=makeQuery(id+"F4.opFillet","BLEND_EDGE",EDGE,{"blendedFrom":[makeQuery(id+"F1.opExtrude","SWEPT_EDGE",EDGE,{"disambiguationData":[OSD([subQ2,subQ1,subQ0])]}),makeQuery(id+"F1.opExtrude","CAP_FACE",FACE,{"disambiguationData":[OSD([subQ2,sQuery(id+"F0.wireOp",EDGE,"E1"),sQuery(id+"F0.wireOp",EDGE,"E5.trimOffspring"),subQ1,sQuery(id+"F0.wireOp",EDGE,"E7"),subQ0,sQuery(id+"F0.wireOp",EDGE,"E11"),sQuery(id+"F0.wireOp",EDGE,"E12"),sQuery(id+"F0.wireOp",EDGE,"E13"),sQuery(id+"F0.wireOp",EDGE,"E14"),sQuery(id+"F0.wireOp",EDGE,"E15"),sQuery(id+"F0.wireOp",EDGE,"E16"),sQuery(id+"F0.wireOp",EDGE,"E17"),sQuery(id+"F0.wireOp",EDGE,"E18"),sQuery(id+"F0.wireOp",EDGE,"E20.1.2"),sQuery(id+"F0.wireOp",EDGE,"E20.1.3"),sQuery(id+"F0.wireOp",EDGE,"E20.1.5"),sQuery(id+"F0.wireOp",EDGE,"E20.1.9"),sQuery(id+"F0.wireOp",EDGE,"E20.1.10"),sQuery(id+"F0.wireOp",EDGE,"E20.1.12"),sQuery(id+"F0.wireOp",EDGE,"E20.1.14"),sQuery(id+"F0.wireOp",EDGE,"E20.1.15"),sQuery(id+"F0.wireOp",EDGE,"E20.1.16"),sQuery(id+"F0.wireOp",EDGE,"E20.1.17"),sQuery(id+"F0.wireOp",EDGE,"E20.1.19"),sQuery(id+"F0.wireOp",EDGE,"E20.1.20"),sQuery(id+"F0.wireOp",EDGE,"E20.2.2"),sQuery(id+"F0.wireOp",EDGE,"E20.2.3"),sQuery(id+"F0.wireOp",EDGE,"E20.2.5"),sQuery(id+"F0.wireOp",EDGE,"E20.2.9"),sQuery(id+"F0.wireOp",EDGE,"E20.2.10"),sQuery(id+"F0.wireOp",EDGE,"E20.2.12"),sQuery(id+"F0.wireOp",EDGE,"E20.2.14"),sQuery(id+"F0.wireOp",EDGE,"E20.2.15"),sQuery(id+"F0.wireOp",EDGE,"E20.2.16"),sQuery(id+"F0.wireOp",EDGE,"E20.2.17"),sQuery(id+"F0.wireOp",EDGE,"E20.2.19"),sQuery(id+"F0.wireOp",EDGE,"E20.2.20")])],"isStart":true})],"blendedInto":[makeQuery(id+"F1.opExtrude","CAP_FACE",FACE,{"disambiguationData":[OSD([subQ2,sQuery(id+"F0.wireOp",EDGE,"E1"),sQuery(id+"F0.wireOp",EDGE,"E5.trimOffspring"),subQ1,sQuery(id+"F0.wireOp",EDGE,"E7"),subQ0,sQuery(id+"F0.wireOp",EDGE,"E11"),sQuery(id+"F0.wireOp",EDGE,"E12"),sQuery(id+"F0.wireOp",EDGE,"E13"),sQuery(id+"F0.wireOp",EDGE,"E14"),sQuery(id+"F0.wireOp",EDGE,"E15"),sQuery(id+"F0.wireOp",EDGE,"E16"),sQuery(id+"F0.wireOp",EDGE,"E17"),sQuery(id+"F0.wireOp",EDGE,"E18"),sQuery(id+"F0.wireOp",EDGE,"E20.1.2"),sQuery(id+"F0.wireOp",EDGE,"E20.1.3"),sQuery(id+"F0.wireOp",EDGE,"E20.1.5"),sQuery(id+"F0.wireOp",EDGE,"E20.1.9"),sQuery(id+"F0.wireOp",EDGE,"E20.1.10"),sQuery(id+"F0.wireOp",EDGE,"E20.1.12"),sQuery(id+"F0.wireOp",EDGE,"E20.1.14"),sQuery(id+"F0.wireOp",EDGE,"E20.1.15"),sQuery(id+"F0.wireOp",EDGE,"E20.1.16"),sQuery(id+"F0.wireOp",EDGE,"E20.1.17"),sQuery(id+"F0.wireOp",EDGE,"E20.1.19"),sQuery(id+"F0.wireOp",EDGE,"E20.1.20"),sQuery(id+"F0.wireOp",EDGE,"E20.2.2"),sQuery(id+"F0.wireOp",EDGE,"E20.2.3"),sQuery(id+"F0.wireOp",EDGE,"E20.2.5"),sQuery(id+"F0.wireOp",EDGE,"E20.2.9"),sQuery(id+"F0.wireOp",EDGE,"E20.2.10"),sQuery(id+"F0.wireOp",EDGE,"E20.2.12"),sQuery(id+"F0.wireOp",EDGE,"E20.2.14"),sQuery(id+"F0.wireOp",EDGE,"E20.2.15"),sQuery(id+"F0.wireOp",EDGE,"E20.2.16"),sQuery(id+"F0.wireOp",EDGE,"E20.2.17"),sQuery(id+"F0.wireOp",EDGE,"E20.2.19"),sQuery(id+"F0.wireOp",EDGE,"E20.2.20")])],"isStart":true})]});}
            var Q8;
            Q8=makeQuery(id+"F1.opExtrude","CAP_EDGE",EDGE,{"disambiguationData":[OSD([sQuery(id+"F0.wireOp",EDGE,"E11")])],"isStart":true});
            var Q9;
            Q9=makeQuery(id+"F1.opExtrude","CAP_EDGE",EDGE,{"disambiguationData":[OSD([sQuery(id+"F0.wireOp",EDGE,"E12")])],"isStart":true});
            var Q10;
            Q10=makeQuery(id+"F1.opExtrude","CAP_EDGE",EDGE,{"disambiguationData":[OSD([sQuery(id+"F0.wireOp",EDGE,"E12")])],"isStart":false});
            var Q11;
            Q11=makeQuery(id+"F1.opExtrude","CAP_EDGE",EDGE,{"disambiguationData":[OSD([sQuery(id+"F0.wireOp",EDGE,"E13")])],"isStart":false});
            var Q12;
            Q12=makeQuery(id+"F1.opExtrude","CAP_EDGE",EDGE,{"disambiguationData":[OSD([sQuery(id+"F0.wireOp",EDGE,"E14")])],"isStart":true});
            var Q13;
            Q13=makeQuery(id+"F1.opExtrude","CAP_EDGE",EDGE,{"disambiguationData":[OSD([sQuery(id+"F0.wireOp",EDGE,"E14")])],"isStart":false});
            var Q14;
            Q14=makeQuery(id+"F1.opExtrude","CAP_EDGE",EDGE,{"disambiguationData":[OSD([sQuery(id+"F0.wireOp",EDGE,"E15")])],"isStart":false});
            var Q15;
            Q15=makeQuery(id+"F1.opExtrude","CAP_EDGE",EDGE,{"disambiguationData":[OSD([sQuery(id+"F0.wireOp",EDGE,"E15")])],"isStart":true});
            var Q16;
            Q16=makeQuery(id+"F1.opExtrude","CAP_EDGE",EDGE,{"disambiguationData":[OSD([sQuery(id+"F0.wireOp",EDGE,"E16")])],"isStart":true});
            var Q17;
            Q17=makeQuery(id+"F1.opExtrude","CAP_EDGE",EDGE,{"disambiguationData":[OSD([sQuery(id+"F0.wireOp",EDGE,"E16")])],"isStart":false});
            var Q18;
            Q18=makeQuery(id+"F1.opExtrude","CAP_EDGE",EDGE,{"disambiguationData":[OSD([sQuery(id+"F0.wireOp",EDGE,"E17")])],"isStart":false});
            var Q19;
            Q19=makeQuery(id+"F1.opExtrude","CAP_EDGE",EDGE,{"disambiguationData":[OSD([sQuery(id+"F0.wireOp",EDGE,"E17")])],"isStart":true});
            var Q20;
            Q20=makeQuery(id+"F1.opExtrude","CAP_EDGE",EDGE,{"disambiguationData":[OSD([sQuery(id+"F0.wireOp",EDGE,"E11")])],"isStart":false});
            var Q21;
            Q21=makeQuery(id+"F1.opExtrude","CAP_EDGE",EDGE,{"disambiguationData":[OSD([sQuery(id+"F0.wireOp",EDGE,"E13")])],"isStart":true});
            var Q22;
            Q22=makeQuery(id+"F1.opExtrude","SWEPT_EDGE",EDGE,{"disambiguationData":[OSD([sQuery(id+"F0.wireOp",EDGE,"E12"),sQuery(id+"F0.wireOp",EDGE,"E13")])]});
            var Q23;
            Q23=makeQuery(id+"F1.opExtrude","SWEPT_EDGE",EDGE,{"disambiguationData":[OSD([sQuery(id+"F0.wireOp",EDGE,"E14"),sQuery(id+"F0.wireOp",EDGE,"E15")])]});
            var Q24;
            Q24=makeQuery(id+"F1.opExtrude","SWEPT_EDGE",EDGE,{"disambiguationData":[OSD([sQuery(id+"F0.wireOp",EDGE,"E16"),sQuery(id+"F0.wireOp",EDGE,"E17")])]});
            var Q25;
            Q25=makeQuery(id+"F4.opFillet","BLEND_EDGE",EDGE,{"blendedFrom":[makeQuery(id+"F1.opExtrude","SWEPT_EDGE",EDGE,{"disambiguationData":[OSD([sQuery(id+"F0.wireOp",EDGE,"E0"),sQuery(id+"F0.wireOp",EDGE,"E6.trimOffspring"),sQuery(id+"F0.wireOp",EDGE,"E10")])]}),makeQuery(id+"F1.opExtrude","SWEPT_FACE",FACE,{"disambiguationData":[OSD([sQuery(id+"F0.wireOp",EDGE,"E11")])]})],"blendedInto":[makeQuery(id+"F1.opExtrude","SWEPT_FACE",FACE,{"disambiguationData":[OSD([sQuery(id+"F0.wireOp",EDGE,"E11")])]})]});
            var Q26;
            Q26=makeQuery(id+"F1.opExtrude","CAP_EDGE",EDGE,{"disambiguationData":[OSD([sQuery(id+"F0.wireOp",EDGE,"E20.2.9")])],"isStart":false});
            var Q27;
            Q27=makeQuery(id+"F1.opExtrude","CAP_EDGE",EDGE,{"disambiguationData":[OSD([sQuery(id+"F0.wireOp",EDGE,"E20.2.9")])],"isStart":true});
            var Q28;
            Q28=makeQuery(id+"F1.opExtrude","CAP_EDGE",EDGE,{"disambiguationData":[OSD([sQuery(id+"F0.wireOp",EDGE,"E20.2.20")])],"isStart":false});
            var Q29;
            Q29=makeQuery(id+"F1.opExtrude","CAP_EDGE",EDGE,{"disambiguationData":[OSD([sQuery(id+"F0.wireOp",EDGE,"E20.2.20")])],"isStart":true});
            var Q30;
            Q30=makeQuery(id+"F1.opExtrude","CAP_EDGE",EDGE,{"disambiguationData":[OSD([sQuery(id+"F0.wireOp",EDGE,"E20.2.16")])],"isStart":false});
            var Q31;
            Q31=makeQuery(id+"F1.opExtrude","CAP_EDGE",EDGE,{"disambiguationData":[OSD([sQuery(id+"F0.wireOp",EDGE,"E20.2.16")])],"isStart":true});
            var Q32;
            Q32=makeQuery(id+"F1.opExtrude","CAP_EDGE",EDGE,{"disambiguationData":[OSD([sQuery(id+"F0.wireOp",EDGE,"E20.2.19")])],"isStart":true});
            var Q33;
            Q33=makeQuery(id+"F1.opExtrude","CAP_EDGE",EDGE,{"disambiguationData":[OSD([sQuery(id+"F0.wireOp",EDGE,"E20.2.19")])],"isStart":false});
            var Q34;
            Q34=makeQuery(id+"F1.opExtrude","CAP_EDGE",EDGE,{"disambiguationData":[OSD([sQuery(id+"F0.wireOp",EDGE,"E20.2.14")])],"isStart":true});
            var Q35;
            Q35=makeQuery(id+"F1.opExtrude","CAP_EDGE",EDGE,{"disambiguationData":[OSD([sQuery(id+"F0.wireOp",EDGE,"E20.2.14")])],"isStart":false});
            var Q36;
            Q36=makeQuery(id+"F1.opExtrude","CAP_EDGE",EDGE,{"disambiguationData":[OSD([sQuery(id+"F0.wireOp",EDGE,"E20.2.15")])],"isStart":true});
            var Q37;
            Q37=makeQuery(id+"F1.opExtrude","CAP_EDGE",EDGE,{"disambiguationData":[OSD([sQuery(id+"F0.wireOp",EDGE,"E20.2.15")])],"isStart":false});
            var Q38;
            Q38=makeQuery(id+"F1.opExtrude","SWEPT_EDGE",EDGE,{"disambiguationData":[OSD([sQuery(id+"F0.wireOp",EDGE,"E20.2.15"),sQuery(id+"F0.wireOp",EDGE,"E20.2.16")])]});
            var Q39;
            Q39=makeQuery(id+"F1.opExtrude","SWEPT_EDGE",EDGE,{"disambiguationData":[OSD([sQuery(id+"F0.wireOp",EDGE,"E20.2.14"),sQuery(id+"F0.wireOp",EDGE,"E20.2.20")])]});
            var Q40;
            Q40=makeQuery(id+"F1.opExtrude","SWEPT_EDGE",EDGE,{"disambiguationData":[OSD([sQuery(id+"F0.wireOp",EDGE,"E20.2.9"),sQuery(id+"F0.wireOp",EDGE,"E20.2.19")])]});
            var Q41;
            Q41=makeQuery(id+"F4.opFillet","BLEND_EDGE",EDGE,{"blendedFrom":[makeQuery(id+"F1.opExtrude","SWEPT_EDGE",EDGE,{"disambiguationData":[OSD([sQuery(id+"F0.wireOp",EDGE,"E0"),sQuery(id+"F0.wireOp",EDGE,"E20.2.2"),sQuery(id+"F0.wireOp",EDGE,"E20.2.3")])]}),makeQuery(id+"F1.opExtrude","SWEPT_FACE",FACE,{"disambiguationData":[OSD([sQuery(id+"F0.wireOp",EDGE,"E20.2.17")])]})],"blendedInto":[makeQuery(id+"F1.opExtrude","SWEPT_FACE",FACE,{"disambiguationData":[OSD([sQuery(id+"F0.wireOp",EDGE,"E20.2.17")])]})]});
            var Q42;
            Q42=makeQuery(id+"F1.opExtrude","CAP_EDGE",EDGE,{"disambiguationData":[OSD([sQuery(id+"F0.wireOp",EDGE,"E20.1.9")])],"isStart":true});
            var Q43;
            Q43=makeQuery(id+"F1.opExtrude","CAP_EDGE",EDGE,{"disambiguationData":[OSD([sQuery(id+"F0.wireOp",EDGE,"E20.1.9")])],"isStart":false});
            var Q44;
            Q44=makeQuery(id+"F1.opExtrude","CAP_EDGE",EDGE,{"disambiguationData":[OSD([sQuery(id+"F0.wireOp",EDGE,"E20.1.20")])],"isStart":true});
            var Q45;
            Q45=makeQuery(id+"F1.opExtrude","CAP_EDGE",EDGE,{"disambiguationData":[OSD([sQuery(id+"F0.wireOp",EDGE,"E20.1.20")])],"isStart":false});
            var Q46;
            Q46=makeQuery(id+"F1.opExtrude","CAP_EDGE",EDGE,{"disambiguationData":[OSD([sQuery(id+"F0.wireOp",EDGE,"E20.1.16")])],"isStart":true});
            var Q47;
            Q47=makeQuery(id+"F1.opExtrude","CAP_EDGE",EDGE,{"disambiguationData":[OSD([sQuery(id+"F0.wireOp",EDGE,"E20.1.16")])],"isStart":false});
            var Q48;
            Q48=makeQuery(id+"F1.opExtrude","CAP_EDGE",EDGE,{"disambiguationData":[OSD([sQuery(id+"F0.wireOp",EDGE,"E20.1.15")])],"isStart":true});
            var Q49;
            Q49=makeQuery(id+"F1.opExtrude","CAP_EDGE",EDGE,{"disambiguationData":[OSD([sQuery(id+"F0.wireOp",EDGE,"E20.1.15")])],"isStart":false});
            var Q50;
            Q50=makeQuery(id+"F1.opExtrude","CAP_EDGE",EDGE,{"disambiguationData":[OSD([sQuery(id+"F0.wireOp",EDGE,"E20.1.14")])],"isStart":false});
            var Q51;
            Q51=makeQuery(id+"F1.opExtrude","CAP_EDGE",EDGE,{"disambiguationData":[OSD([sQuery(id+"F0.wireOp",EDGE,"E20.1.14")])],"isStart":true});
            var Q52;
            Q52=makeQuery(id+"F1.opExtrude","CAP_EDGE",EDGE,{"disambiguationData":[OSD([sQuery(id+"F0.wireOp",EDGE,"E20.1.19")])],"isStart":true});
            var Q53;
            Q53=makeQuery(id+"F1.opExtrude","CAP_EDGE",EDGE,{"disambiguationData":[OSD([sQuery(id+"F0.wireOp",EDGE,"E20.1.19")])],"isStart":false});
            var Q54;
            Q54=makeQuery(id+"F1.opExtrude","SWEPT_EDGE",EDGE,{"disambiguationData":[OSD([sQuery(id+"F0.wireOp",EDGE,"E20.1.9"),sQuery(id+"F0.wireOp",EDGE,"E20.1.19")])]});
            var Q55;
            Q55=makeQuery(id+"F1.opExtrude","SWEPT_EDGE",EDGE,{"disambiguationData":[OSD([sQuery(id+"F0.wireOp",EDGE,"E20.1.14"),sQuery(id+"F0.wireOp",EDGE,"E20.1.20")])]});
            var Q56;
            Q56=makeQuery(id+"F1.opExtrude","SWEPT_EDGE",EDGE,{"disambiguationData":[OSD([sQuery(id+"F0.wireOp",EDGE,"E20.1.15"),sQuery(id+"F0.wireOp",EDGE,"E20.1.16")])]});
            var Q57;
            {var subQ0=sQuery(id+"F0.wireOp",EDGE,"E20.1.3");var subQ1=sQuery(id+"F0.wireOp",EDGE,"E20.1.2");var subQ2=sQuery(id+"F0.wireOp",EDGE,"E0");Q57=makeQuery(id+"F4.opFillet","BLEND_EDGE",EDGE,{"disambiguationData":[OD(1.0)],"blendedFrom":[makeQuery(id+"F1.opExtrude","SWEPT_EDGE",EDGE,{"disambiguationData":[OSD([subQ2,subQ1,subQ0])]}),makeQuery(id+"F1.opExtrude","CAP_FACE",FACE,{"disambiguationData":[OSD([subQ2,sQuery(id+"F0.wireOp",EDGE,"E1"),sQuery(id+"F0.wireOp",EDGE,"E5.trimOffspring"),sQuery(id+"F0.wireOp",EDGE,"E6.trimOffspring"),sQuery(id+"F0.wireOp",EDGE,"E7"),sQuery(id+"F0.wireOp",EDGE,"E10"),sQuery(id+"F0.wireOp",EDGE,"E11"),sQuery(id+"F0.wireOp",EDGE,"E12"),sQuery(id+"F0.wireOp",EDGE,"E13"),sQuery(id+"F0.wireOp",EDGE,"E14"),sQuery(id+"F0.wireOp",EDGE,"E15"),sQuery(id+"F0.wireOp",EDGE,"E16"),sQuery(id+"F0.wireOp",EDGE,"E17"),sQuery(id+"F0.wireOp",EDGE,"E18"),subQ1,subQ0,sQuery(id+"F0.wireOp",EDGE,"E20.1.5"),sQuery(id+"F0.wireOp",EDGE,"E20.1.9"),sQuery(id+"F0.wireOp",EDGE,"E20.1.10"),sQuery(id+"F0.wireOp",EDGE,"E20.1.12"),sQuery(id+"F0.wireOp",EDGE,"E20.1.14"),sQuery(id+"F0.wireOp",EDGE,"E20.1.15"),sQuery(id+"F0.wireOp",EDGE,"E20.1.16"),sQuery(id+"F0.wireOp",EDGE,"E20.1.17"),sQuery(id+"F0.wireOp",EDGE,"E20.1.19"),sQuery(id+"F0.wireOp",EDGE,"E20.1.20"),sQuery(id+"F0.wireOp",EDGE,"E20.2.2"),sQuery(id+"F0.wireOp",EDGE,"E20.2.3"),sQuery(id+"F0.wireOp",EDGE,"E20.2.5"),sQuery(id+"F0.wireOp",EDGE,"E20.2.9"),sQuery(id+"F0.wireOp",EDGE,"E20.2.10"),sQuery(id+"F0.wireOp",EDGE,"E20.2.12"),sQuery(id+"F0.wireOp",EDGE,"E20.2.14"),sQuery(id+"F0.wireOp",EDGE,"E20.2.15"),sQuery(id+"F0.wireOp",EDGE,"E20.2.16"),sQuery(id+"F0.wireOp",EDGE,"E20.2.17"),sQuery(id+"F0.wireOp",EDGE,"E20.2.19"),sQuery(id+"F0.wireOp",EDGE,"E20.2.20")])],"isStart":false})],"blendedInto":[makeQuery(id+"F1.opExtrude","CAP_FACE",FACE,{"disambiguationData":[OSD([subQ2,sQuery(id+"F0.wireOp",EDGE,"E1"),sQuery(id+"F0.wireOp",EDGE,"E5.trimOffspring"),sQuery(id+"F0.wireOp",EDGE,"E6.trimOffspring"),sQuery(id+"F0.wireOp",EDGE,"E7"),sQuery(id+"F0.wireOp",EDGE,"E10"),sQuery(id+"F0.wireOp",EDGE,"E11"),sQuery(id+"F0.wireOp",EDGE,"E12"),sQuery(id+"F0.wireOp",EDGE,"E13"),sQuery(id+"F0.wireOp",EDGE,"E14"),sQuery(id+"F0.wireOp",EDGE,"E15"),sQuery(id+"F0.wireOp",EDGE,"E16"),sQuery(id+"F0.wireOp",EDGE,"E17"),sQuery(id+"F0.wireOp",EDGE,"E18"),subQ1,subQ0,sQuery(id+"F0.wireOp",EDGE,"E20.1.5"),sQuery(id+"F0.wireOp",EDGE,"E20.1.9"),sQuery(id+"F0.wireOp",EDGE,"E20.1.10"),sQuery(id+"F0.wireOp",EDGE,"E20.1.12"),sQuery(id+"F0.wireOp",EDGE,"E20.1.14"),sQuery(id+"F0.wireOp",EDGE,"E20.1.15"),sQuery(id+"F0.wireOp",EDGE,"E20.1.16"),sQuery(id+"F0.wireOp",EDGE,"E20.1.17"),sQuery(id+"F0.wireOp",EDGE,"E20.1.19"),sQuery(id+"F0.wireOp",EDGE,"E20.1.20"),sQuery(id+"F0.wireOp",EDGE,"E20.2.2"),sQuery(id+"F0.wireOp",EDGE,"E20.2.3"),sQuery(id+"F0.wireOp",EDGE,"E20.2.5"),sQuery(id+"F0.wireOp",EDGE,"E20.2.9"),sQuery(id+"F0.wireOp",EDGE,"E20.2.10"),sQuery(id+"F0.wireOp",EDGE,"E20.2.12"),sQuery(id+"F0.wireOp",EDGE,"E20.2.14"),sQuery(id+"F0.wireOp",EDGE,"E20.2.15"),sQuery(id+"F0.wireOp",EDGE,"E20.2.16"),sQuery(id+"F0.wireOp",EDGE,"E20.2.17"),sQuery(id+"F0.wireOp",EDGE,"E20.2.19"),sQuery(id+"F0.wireOp",EDGE,"E20.2.20")])],"isStart":false})]});}
            var Q58;
            {var subQ0=sQuery(id+"F0.wireOp",EDGE,"E20.1.3");var subQ1=sQuery(id+"F0.wireOp",EDGE,"E20.1.2");var subQ2=sQuery(id+"F0.wireOp",EDGE,"E0");Q58=makeQuery(id+"F4.opFillet","BLEND_EDGE",EDGE,{"disambiguationData":[OD(1.0)],"blendedFrom":[makeQuery(id+"F1.opExtrude","SWEPT_EDGE",EDGE,{"disambiguationData":[OSD([subQ2,subQ1,subQ0])]}),makeQuery(id+"F1.opExtrude","CAP_FACE",FACE,{"disambiguationData":[OSD([subQ2,sQuery(id+"F0.wireOp",EDGE,"E1"),sQuery(id+"F0.wireOp",EDGE,"E5.trimOffspring"),sQuery(id+"F0.wireOp",EDGE,"E6.trimOffspring"),sQuery(id+"F0.wireOp",EDGE,"E7"),sQuery(id+"F0.wireOp",EDGE,"E10"),sQuery(id+"F0.wireOp",EDGE,"E11"),sQuery(id+"F0.wireOp",EDGE,"E12"),sQuery(id+"F0.wireOp",EDGE,"E13"),sQuery(id+"F0.wireOp",EDGE,"E14"),sQuery(id+"F0.wireOp",EDGE,"E15"),sQuery(id+"F0.wireOp",EDGE,"E16"),sQuery(id+"F0.wireOp",EDGE,"E17"),sQuery(id+"F0.wireOp",EDGE,"E18"),subQ1,subQ0,sQuery(id+"F0.wireOp",EDGE,"E20.1.5"),sQuery(id+"F0.wireOp",EDGE,"E20.1.9"),sQuery(id+"F0.wireOp",EDGE,"E20.1.10"),sQuery(id+"F0.wireOp",EDGE,"E20.1.12"),sQuery(id+"F0.wireOp",EDGE,"E20.1.14"),sQuery(id+"F0.wireOp",EDGE,"E20.1.15"),sQuery(id+"F0.wireOp",EDGE,"E20.1.16"),sQuery(id+"F0.wireOp",EDGE,"E20.1.17"),sQuery(id+"F0.wireOp",EDGE,"E20.1.19"),sQuery(id+"F0.wireOp",EDGE,"E20.1.20"),sQuery(id+"F0.wireOp",EDGE,"E20.2.2"),sQuery(id+"F0.wireOp",EDGE,"E20.2.3"),sQuery(id+"F0.wireOp",EDGE,"E20.2.5"),sQuery(id+"F0.wireOp",EDGE,"E20.2.9"),sQuery(id+"F0.wireOp",EDGE,"E20.2.10"),sQuery(id+"F0.wireOp",EDGE,"E20.2.12"),sQuery(id+"F0.wireOp",EDGE,"E20.2.14"),sQuery(id+"F0.wireOp",EDGE,"E20.2.15"),sQuery(id+"F0.wireOp",EDGE,"E20.2.16"),sQuery(id+"F0.wireOp",EDGE,"E20.2.17"),sQuery(id+"F0.wireOp",EDGE,"E20.2.19"),sQuery(id+"F0.wireOp",EDGE,"E20.2.20")])],"isStart":true})],"blendedInto":[makeQuery(id+"F1.opExtrude","CAP_FACE",FACE,{"disambiguationData":[OSD([subQ2,sQuery(id+"F0.wireOp",EDGE,"E1"),sQuery(id+"F0.wireOp",EDGE,"E5.trimOffspring"),sQuery(id+"F0.wireOp",EDGE,"E6.trimOffspring"),sQuery(id+"F0.wireOp",EDGE,"E7"),sQuery(id+"F0.wireOp",EDGE,"E10"),sQuery(id+"F0.wireOp",EDGE,"E11"),sQuery(id+"F0.wireOp",EDGE,"E12"),sQuery(id+"F0.wireOp",EDGE,"E13"),sQuery(id+"F0.wireOp",EDGE,"E14"),sQuery(id+"F0.wireOp",EDGE,"E15"),sQuery(id+"F0.wireOp",EDGE,"E16"),sQuery(id+"F0.wireOp",EDGE,"E17"),sQuery(id+"F0.wireOp",EDGE,"E18"),subQ1,subQ0,sQuery(id+"F0.wireOp",EDGE,"E20.1.5"),sQuery(id+"F0.wireOp",EDGE,"E20.1.9"),sQuery(id+"F0.wireOp",EDGE,"E20.1.10"),sQuery(id+"F0.wireOp",EDGE,"E20.1.12"),sQuery(id+"F0.wireOp",EDGE,"E20.1.14"),sQuery(id+"F0.wireOp",EDGE,"E20.1.15"),sQuery(id+"F0.wireOp",EDGE,"E20.1.16"),sQuery(id+"F0.wireOp",EDGE,"E20.1.17"),sQuery(id+"F0.wireOp",EDGE,"E20.1.19"),sQuery(id+"F0.wireOp",EDGE,"E20.1.20"),sQuery(id+"F0.wireOp",EDGE,"E20.2.2"),sQuery(id+"F0.wireOp",EDGE,"E20.2.3"),sQuery(id+"F0.wireOp",EDGE,"E20.2.5"),sQuery(id+"F0.wireOp",EDGE,"E20.2.9"),sQuery(id+"F0.wireOp",EDGE,"E20.2.10"),sQuery(id+"F0.wireOp",EDGE,"E20.2.12"),sQuery(id+"F0.wireOp",EDGE,"E20.2.14"),sQuery(id+"F0.wireOp",EDGE,"E20.2.15"),sQuery(id+"F0.wireOp",EDGE,"E20.2.16"),sQuery(id+"F0.wireOp",EDGE,"E20.2.17"),sQuery(id+"F0.wireOp",EDGE,"E20.2.19"),sQuery(id+"F0.wireOp",EDGE,"E20.2.20")])],"isStart":true})]});}
            var Q59;
            {var subQ0=sQuery(id+"F0.wireOp",EDGE,"E20.2.3");var subQ1=sQuery(id+"F0.wireOp",EDGE,"E20.2.2");var subQ2=sQuery(id+"F0.wireOp",EDGE,"E0");Q59=makeQuery(id+"F4.opFillet","BLEND_EDGE",EDGE,{"disambiguationData":[OD(1.0)],"blendedFrom":[makeQuery(id+"F1.opExtrude","SWEPT_EDGE",EDGE,{"disambiguationData":[OSD([subQ2,subQ1,subQ0])]}),makeQuery(id+"F1.opExtrude","CAP_FACE",FACE,{"disambiguationData":[OSD([subQ2,sQuery(id+"F0.wireOp",EDGE,"E1"),sQuery(id+"F0.wireOp",EDGE,"E5.trimOffspring"),sQuery(id+"F0.wireOp",EDGE,"E6.trimOffspring"),sQuery(id+"F0.wireOp",EDGE,"E7"),sQuery(id+"F0.wireOp",EDGE,"E10"),sQuery(id+"F0.wireOp",EDGE,"E11"),sQuery(id+"F0.wireOp",EDGE,"E12"),sQuery(id+"F0.wireOp",EDGE,"E13"),sQuery(id+"F0.wireOp",EDGE,"E14"),sQuery(id+"F0.wireOp",EDGE,"E15"),sQuery(id+"F0.wireOp",EDGE,"E16"),sQuery(id+"F0.wireOp",EDGE,"E17"),sQuery(id+"F0.wireOp",EDGE,"E18"),sQuery(id+"F0.wireOp",EDGE,"E20.1.2"),sQuery(id+"F0.wireOp",EDGE,"E20.1.3"),sQuery(id+"F0.wireOp",EDGE,"E20.1.5"),sQuery(id+"F0.wireOp",EDGE,"E20.1.9"),sQuery(id+"F0.wireOp",EDGE,"E20.1.10"),sQuery(id+"F0.wireOp",EDGE,"E20.1.12"),sQuery(id+"F0.wireOp",EDGE,"E20.1.14"),sQuery(id+"F0.wireOp",EDGE,"E20.1.15"),sQuery(id+"F0.wireOp",EDGE,"E20.1.16"),sQuery(id+"F0.wireOp",EDGE,"E20.1.17"),sQuery(id+"F0.wireOp",EDGE,"E20.1.19"),sQuery(id+"F0.wireOp",EDGE,"E20.1.20"),subQ1,subQ0,sQuery(id+"F0.wireOp",EDGE,"E20.2.5"),sQuery(id+"F0.wireOp",EDGE,"E20.2.9"),sQuery(id+"F0.wireOp",EDGE,"E20.2.10"),sQuery(id+"F0.wireOp",EDGE,"E20.2.12"),sQuery(id+"F0.wireOp",EDGE,"E20.2.14"),sQuery(id+"F0.wireOp",EDGE,"E20.2.15"),sQuery(id+"F0.wireOp",EDGE,"E20.2.16"),sQuery(id+"F0.wireOp",EDGE,"E20.2.17"),sQuery(id+"F0.wireOp",EDGE,"E20.2.19"),sQuery(id+"F0.wireOp",EDGE,"E20.2.20")])],"isStart":false})],"blendedInto":[makeQuery(id+"F1.opExtrude","CAP_FACE",FACE,{"disambiguationData":[OSD([subQ2,sQuery(id+"F0.wireOp",EDGE,"E1"),sQuery(id+"F0.wireOp",EDGE,"E5.trimOffspring"),sQuery(id+"F0.wireOp",EDGE,"E6.trimOffspring"),sQuery(id+"F0.wireOp",EDGE,"E7"),sQuery(id+"F0.wireOp",EDGE,"E10"),sQuery(id+"F0.wireOp",EDGE,"E11"),sQuery(id+"F0.wireOp",EDGE,"E12"),sQuery(id+"F0.wireOp",EDGE,"E13"),sQuery(id+"F0.wireOp",EDGE,"E14"),sQuery(id+"F0.wireOp",EDGE,"E15"),sQuery(id+"F0.wireOp",EDGE,"E16"),sQuery(id+"F0.wireOp",EDGE,"E17"),sQuery(id+"F0.wireOp",EDGE,"E18"),sQuery(id+"F0.wireOp",EDGE,"E20.1.2"),sQuery(id+"F0.wireOp",EDGE,"E20.1.3"),sQuery(id+"F0.wireOp",EDGE,"E20.1.5"),sQuery(id+"F0.wireOp",EDGE,"E20.1.9"),sQuery(id+"F0.wireOp",EDGE,"E20.1.10"),sQuery(id+"F0.wireOp",EDGE,"E20.1.12"),sQuery(id+"F0.wireOp",EDGE,"E20.1.14"),sQuery(id+"F0.wireOp",EDGE,"E20.1.15"),sQuery(id+"F0.wireOp",EDGE,"E20.1.16"),sQuery(id+"F0.wireOp",EDGE,"E20.1.17"),sQuery(id+"F0.wireOp",EDGE,"E20.1.19"),sQuery(id+"F0.wireOp",EDGE,"E20.1.20"),subQ1,subQ0,sQuery(id+"F0.wireOp",EDGE,"E20.2.5"),sQuery(id+"F0.wireOp",EDGE,"E20.2.9"),sQuery(id+"F0.wireOp",EDGE,"E20.2.10"),sQuery(id+"F0.wireOp",EDGE,"E20.2.12"),sQuery(id+"F0.wireOp",EDGE,"E20.2.14"),sQuery(id+"F0.wireOp",EDGE,"E20.2.15"),sQuery(id+"F0.wireOp",EDGE,"E20.2.16"),sQuery(id+"F0.wireOp",EDGE,"E20.2.17"),sQuery(id+"F0.wireOp",EDGE,"E20.2.19"),sQuery(id+"F0.wireOp",EDGE,"E20.2.20")])],"isStart":false})]});}
            var Q60;
            {var subQ0=sQuery(id+"F0.wireOp",EDGE,"E20.2.3");var subQ1=sQuery(id+"F0.wireOp",EDGE,"E20.2.2");var subQ2=sQuery(id+"F0.wireOp",EDGE,"E0");Q60=makeQuery(id+"F4.opFillet","BLEND_EDGE",EDGE,{"disambiguationData":[OD(1.0)],"blendedFrom":[makeQuery(id+"F1.opExtrude","SWEPT_EDGE",EDGE,{"disambiguationData":[OSD([subQ2,subQ1,subQ0])]}),makeQuery(id+"F1.opExtrude","CAP_FACE",FACE,{"disambiguationData":[OSD([subQ2,sQuery(id+"F0.wireOp",EDGE,"E1"),sQuery(id+"F0.wireOp",EDGE,"E5.trimOffspring"),sQuery(id+"F0.wireOp",EDGE,"E6.trimOffspring"),sQuery(id+"F0.wireOp",EDGE,"E7"),sQuery(id+"F0.wireOp",EDGE,"E10"),sQuery(id+"F0.wireOp",EDGE,"E11"),sQuery(id+"F0.wireOp",EDGE,"E12"),sQuery(id+"F0.wireOp",EDGE,"E13"),sQuery(id+"F0.wireOp",EDGE,"E14"),sQuery(id+"F0.wireOp",EDGE,"E15"),sQuery(id+"F0.wireOp",EDGE,"E16"),sQuery(id+"F0.wireOp",EDGE,"E17"),sQuery(id+"F0.wireOp",EDGE,"E18"),sQuery(id+"F0.wireOp",EDGE,"E20.1.2"),sQuery(id+"F0.wireOp",EDGE,"E20.1.3"),sQuery(id+"F0.wireOp",EDGE,"E20.1.5"),sQuery(id+"F0.wireOp",EDGE,"E20.1.9"),sQuery(id+"F0.wireOp",EDGE,"E20.1.10"),sQuery(id+"F0.wireOp",EDGE,"E20.1.12"),sQuery(id+"F0.wireOp",EDGE,"E20.1.14"),sQuery(id+"F0.wireOp",EDGE,"E20.1.15"),sQuery(id+"F0.wireOp",EDGE,"E20.1.16"),sQuery(id+"F0.wireOp",EDGE,"E20.1.17"),sQuery(id+"F0.wireOp",EDGE,"E20.1.19"),sQuery(id+"F0.wireOp",EDGE,"E20.1.20"),subQ1,subQ0,sQuery(id+"F0.wireOp",EDGE,"E20.2.5"),sQuery(id+"F0.wireOp",EDGE,"E20.2.9"),sQuery(id+"F0.wireOp",EDGE,"E20.2.10"),sQuery(id+"F0.wireOp",EDGE,"E20.2.12"),sQuery(id+"F0.wireOp",EDGE,"E20.2.14"),sQuery(id+"F0.wireOp",EDGE,"E20.2.15"),sQuery(id+"F0.wireOp",EDGE,"E20.2.16"),sQuery(id+"F0.wireOp",EDGE,"E20.2.17"),sQuery(id+"F0.wireOp",EDGE,"E20.2.19"),sQuery(id+"F0.wireOp",EDGE,"E20.2.20")])],"isStart":true})],"blendedInto":[makeQuery(id+"F1.opExtrude","CAP_FACE",FACE,{"disambiguationData":[OSD([subQ2,sQuery(id+"F0.wireOp",EDGE,"E1"),sQuery(id+"F0.wireOp",EDGE,"E5.trimOffspring"),sQuery(id+"F0.wireOp",EDGE,"E6.trimOffspring"),sQuery(id+"F0.wireOp",EDGE,"E7"),sQuery(id+"F0.wireOp",EDGE,"E10"),sQuery(id+"F0.wireOp",EDGE,"E11"),sQuery(id+"F0.wireOp",EDGE,"E12"),sQuery(id+"F0.wireOp",EDGE,"E13"),sQuery(id+"F0.wireOp",EDGE,"E14"),sQuery(id+"F0.wireOp",EDGE,"E15"),sQuery(id+"F0.wireOp",EDGE,"E16"),sQuery(id+"F0.wireOp",EDGE,"E17"),sQuery(id+"F0.wireOp",EDGE,"E18"),sQuery(id+"F0.wireOp",EDGE,"E20.1.2"),sQuery(id+"F0.wireOp",EDGE,"E20.1.3"),sQuery(id+"F0.wireOp",EDGE,"E20.1.5"),sQuery(id+"F0.wireOp",EDGE,"E20.1.9"),sQuery(id+"F0.wireOp",EDGE,"E20.1.10"),sQuery(id+"F0.wireOp",EDGE,"E20.1.12"),sQuery(id+"F0.wireOp",EDGE,"E20.1.14"),sQuery(id+"F0.wireOp",EDGE,"E20.1.15"),sQuery(id+"F0.wireOp",EDGE,"E20.1.16"),sQuery(id+"F0.wireOp",EDGE,"E20.1.17"),sQuery(id+"F0.wireOp",EDGE,"E20.1.19"),sQuery(id+"F0.wireOp",EDGE,"E20.1.20"),subQ1,subQ0,sQuery(id+"F0.wireOp",EDGE,"E20.2.5"),sQuery(id+"F0.wireOp",EDGE,"E20.2.9"),sQuery(id+"F0.wireOp",EDGE,"E20.2.10"),sQuery(id+"F0.wireOp",EDGE,"E20.2.12"),sQuery(id+"F0.wireOp",EDGE,"E20.2.14"),sQuery(id+"F0.wireOp",EDGE,"E20.2.15"),sQuery(id+"F0.wireOp",EDGE,"E20.2.16"),sQuery(id+"F0.wireOp",EDGE,"E20.2.17"),sQuery(id+"F0.wireOp",EDGE,"E20.2.19"),sQuery(id+"F0.wireOp",EDGE,"E20.2.20")])],"isStart":true})]});}
            var Q61;
            Q61=makeQuery(id+"F1.opExtrude","CAP_EDGE",EDGE,{"disambiguationData":[OSD([sQuery(id+"F0.wireOp",EDGE,"E20.2.17")])],"isStart":false});
            var Q62;
            Q62=makeQuery(id+"F1.opExtrude","CAP_EDGE",EDGE,{"disambiguationData":[OSD([sQuery(id+"F0.wireOp",EDGE,"E20.2.17")])],"isStart":true});
            var Q63;
            Q63=makeQuery(id+"F1.opExtrude","CAP_EDGE",EDGE,{"disambiguationData":[OSD([sQuery(id+"F0.wireOp",EDGE,"E20.1.17")])],"isStart":false});
            var Q64;
            Q64=makeQuery(id+"F1.opExtrude","CAP_EDGE",EDGE,{"disambiguationData":[OSD([sQuery(id+"F0.wireOp",EDGE,"E20.1.17")])],"isStart":true});
            var Q65;
            Q65=makeQuery(id+"F4.opFillet","BLEND_EDGE",EDGE,{"blendedFrom":[makeQuery(id+"F1.opExtrude","SWEPT_EDGE",EDGE,{"disambiguationData":[OSD([sQuery(id+"F0.wireOp",EDGE,"E0"),sQuery(id+"F0.wireOp",EDGE,"E20.1.2"),sQuery(id+"F0.wireOp",EDGE,"E20.1.3")])]}),makeQuery(id+"F1.opExtrude","SWEPT_FACE",FACE,{"disambiguationData":[OSD([sQuery(id+"F0.wireOp",EDGE,"E20.1.17")])]})],"blendedInto":[makeQuery(id+"F1.opExtrude","SWEPT_FACE",FACE,{"disambiguationData":[OSD([sQuery(id+"F0.wireOp",EDGE,"E20.1.17")])]})]});
            fillet(context, id + "F5", {"entities" : qUnion([Q0, Q1, Q2, Q3, Q4, Q5, Q6, Q7, Q8, Q9, Q10, Q11, Q12, Q13, Q14, Q15, Q16, Q17, Q18, Q19, Q20, Q21, Q22, Q23, Q24, Q25, Q26, Q27, Q28, Q29, Q30, Q31, Q32, Q33, Q34, Q35, Q36, Q37, Q38, Q39, Q40, Q41, Q42, Q43, Q44, Q45, Q46, Q47, Q48, Q49, Q50, Q51, Q52, Q53, Q54, Q55, Q56, Q57, Q58, Q59, Q60, Q61, Q62, Q63, Q64, Q65]), "radius" : 2 * mm, "tangentPropagation" : true, "allowEdgeOverflow" : false});
        }
    });
